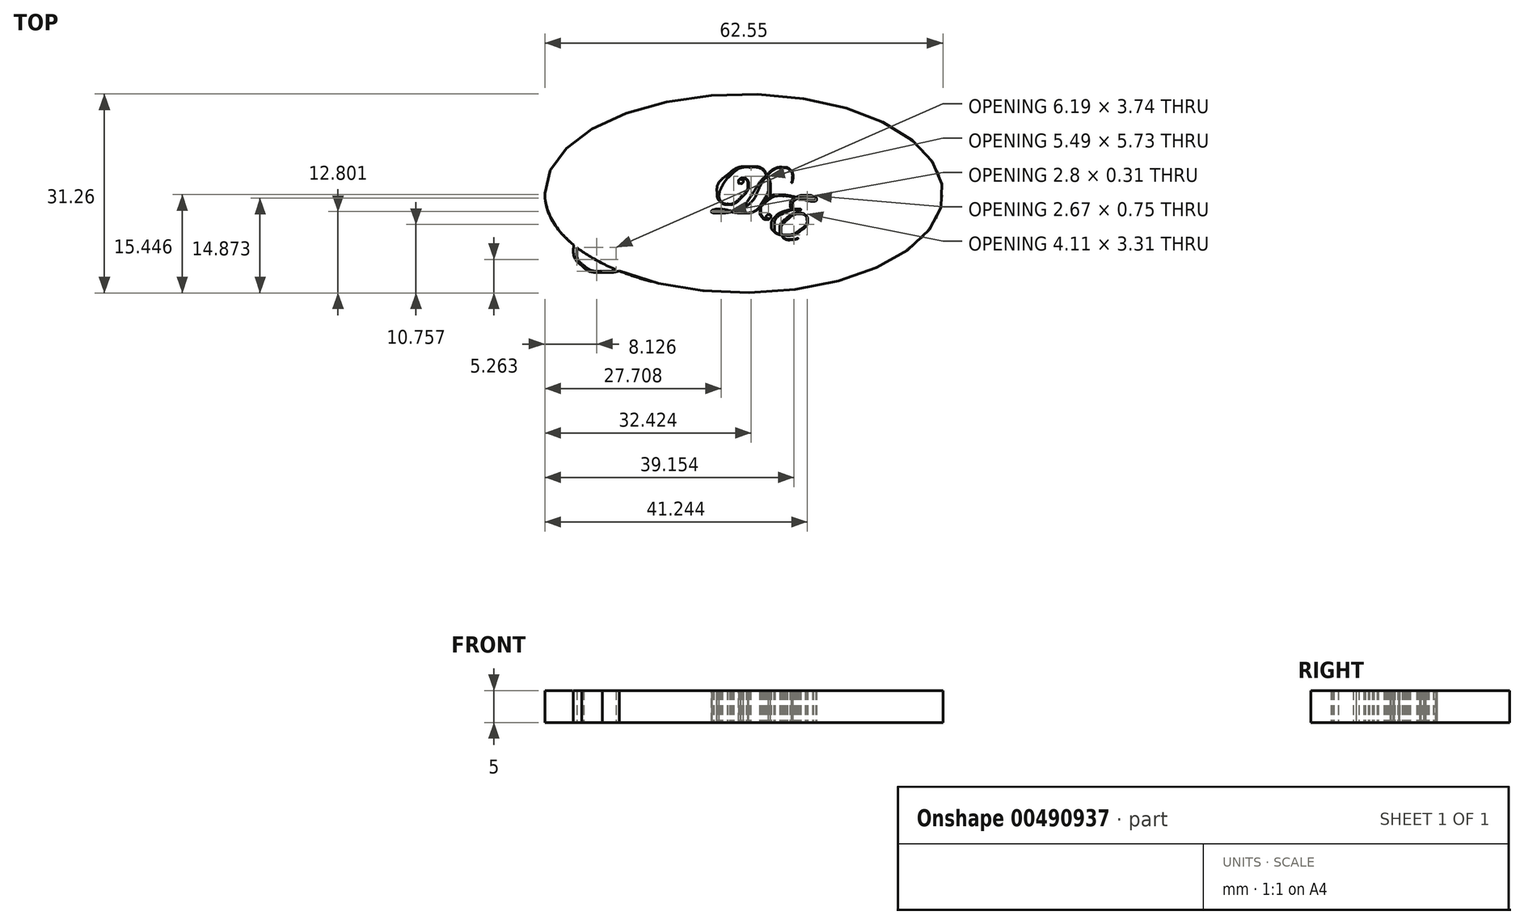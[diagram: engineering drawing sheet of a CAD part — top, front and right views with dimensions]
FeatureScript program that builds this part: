
annotation { "Feature Type Name" : "Feature", "Feature Type Description" : "" }
export const myFeature = defineFeature(function(context is Context, id is Id, definition is map)
    precondition{}
    {
        {
            var Q0;
            Q0=qCreatedBy(makeId("Top.planeOp"),FACE);
            var sketch = newSketch(context, id + "F0", { "sketchPlane" : qUnion([Q0])});
            skFitSpline(sketch, "E0", {"points": [v(-4.56, 0.21) * mm, v(-4.56, 0.16) * mm, v(-4.64, 0.03) * mm, v(-4.81, -0.17) * mm]});
            skFitSpline(sketch, "E1", {"points": [v(-4.81, -0.17) * mm, v(-4.98, -0.37) * mm, v(-5.15, -0.55) * mm, v(-5.33, -0.7) * mm]});
            skFitSpline(sketch, "E2", {"points": [v(-5.33, -0.7) * mm, v(-5.48, -0.94) * mm, v(-5.6, -1.15) * mm, v(-5.67, -1.31) * mm]});
            skFitSpline(sketch, "E3", {"points": [v(-5.67, -1.31) * mm, v(-5.74, -1.47) * mm, v(-5.83, -1.73) * mm, v(-5.94, -2.08) * mm]});
            skFitSpline(sketch, "E4", {"points": [v(-5.94, -2.08) * mm, v(-6.07, -2.51) * mm, v(-6.23, -2.85) * mm, v(-6.43, -3.1) * mm]});
            skFitSpline(sketch, "E5", {"points": [v(-6.43, -3.1) * mm, v(-6.63, -3.36) * mm, v(-6.9, -3.58) * mm, v(-7.25, -3.78) * mm]});
            skFitSpline(sketch, "E6", {"points": [v(-7.25, -3.78) * mm, v(-7.76, -4.06) * mm, v(-8.28, -4.2) * mm, v(-8.81, -4.2) * mm]});
            skFitSpline(sketch, "E7", {"points": [v(-8.81, -4.2) * mm, v(-9.26, -4.2) * mm, v(-9.63, -4.08) * mm, v(-9.9, -3.83) * mm]});
            skFitSpline(sketch, "E8", {"points": [v(-9.9, -3.83) * mm, v(-10.18, -3.59) * mm, v(-10.32, -3.27) * mm, v(-10.32, -2.87) * mm]});
            skFitSpline(sketch, "E9", {"points": [v(-10.32, -2.87) * mm, v(-10.32, -2.53) * mm, v(-10.22, -2.2) * mm, v(-10, -1.9) * mm]});
            skFitSpline(sketch, "E10", {"points": [v(-10, -1.9) * mm, v(-9.8, -1.6) * mm, v(-9.51, -1.35) * mm, v(-9.15, -1.16) * mm]});
            skFitSpline(sketch, "E11", {"points": [v(-9.15, -1.16) * mm, v(-8.78, -0.97) * mm, v(-8.45, -0.88) * mm, v(-8.13, -0.88) * mm]});
            skFitSpline(sketch, "E12", {"points": [v(-8.13, -0.88) * mm, v(-8.1, -0.88) * mm, v(-8.09, -0.88) * mm, v(-8.07, -0.89) * mm]});
            skFitSpline(sketch, "E13", {"points": [v(-8.07, -0.89) * mm, v(-8.07, -0.83) * mm, v(-8.05, -0.73) * mm, v(-8.02, -0.6) * mm]});
            skFitSpline(sketch, "E14", {"points": [v(-8.02, -0.6) * mm, v(-8.06, -0.6) * mm, v(-8.1, -0.6) * mm, v(-8.16, -0.6) * mm]});
            skFitSpline(sketch, "E15", {"points": [v(-8.16, -0.6) * mm, v(-8.51, -0.6) * mm, v(-8.8, -0.53) * mm, v(-9, -0.37) * mm]});
            skFitSpline(sketch, "E16", {"points": [v(-9, -0.37) * mm, v(-9.21, -0.22) * mm, v(-9.32, 0) * mm, v(-9.32, 0.25) * mm]});
            skFitSpline(sketch, "E17", {"points": [v(-9.32, 0.25) * mm, v(-9.32, 0.7) * mm, v(-9.06, 1.1) * mm, v(-8.56, 1.44) * mm]});
            skFitSpline(sketch, "E18", {"points": [v(-8.56, 1.44) * mm, v(-8.05, 1.78) * mm, v(-7.47, 1.96) * mm, v(-6.82, 1.96) * mm]});
            skFitSpline(sketch, "E19", {"points": [v(-6.82, 1.96) * mm, v(-6.3, 1.96) * mm, v(-5.87, 1.83) * mm, v(-5.54, 1.57) * mm]});
            skFitSpline(sketch, "E20", {"points": [v(-5.54, 1.57) * mm, v(-5.3, 1.65) * mm, v(-5.14, 1.7) * mm, v(-5.03, 1.7) * mm]});
            skFitSpline(sketch, "E21", {"points": [v(-5.03, 1.7) * mm, v(-4.82, 1.7) * mm, v(-4.71, 1.6) * mm, v(-4.71, 1.43) * mm]});
            skFitSpline(sketch, "E22", {"points": [v(-4.71, 1.43) * mm, v(-4.71, 1.27) * mm, v(-4.84, 1.07) * mm, v(-5.08, 0.83) * mm]});
            skFitSpline(sketch, "E23", {"points": [v(-5.08, 0.83) * mm, v(-5.07, 0.7) * mm, v(-5.06, 0.6) * mm, v(-5.06, 0.53) * mm]});
            skFitSpline(sketch, "E24", {"points": [v(-5.06, 0.53) * mm, v(-5.06, 0.29) * mm, v(-5.13, 0.04) * mm, v(-5.26, -0.23) * mm]});
            skFitSpline(sketch, "E25", {"points": [v(-5.26, -0.23) * mm, v(-5.3, -0.31) * mm, v(-5.33, -0.35) * mm, v(-5.35, -0.35) * mm]});
            skFitSpline(sketch, "E26", {"points": [v(-5.35, -0.35) * mm, v(-5.36, -0.35) * mm, v(-5.37, -0.35) * mm, v(-5.37, -0.33) * mm]});
            skFitSpline(sketch, "E27", {"points": [v(-5.37, -0.33) * mm, v(-5.37, -0.32) * mm, v(-5.36, -0.31) * mm, v(-5.36, -0.3) * mm]});
            skFitSpline(sketch, "E28", {"points": [v(-5.36, -0.3) * mm, v(-5.2, -0.03) * mm, v(-5.12, 0.25) * mm, v(-5.12, 0.54) * mm]});
            skFitSpline(sketch, "E29", {"points": [v(-5.12, 0.54) * mm, v(-5.12, 0.63) * mm, v(-5.12, 0.71) * mm, v(-5.13, 0.79) * mm]});
            skFitSpline(sketch, "E30", {"points": [v(-5.13, 0.79) * mm, v(-5.5, 0.47) * mm, v(-5.9, 0.19) * mm, v(-6.35, -0.06) * mm]});
            skFitSpline(sketch, "E31", {"points": [v(-6.35, -0.06) * mm, v(-6.8, -0.3) * mm, v(-7.23, -0.46) * mm, v(-7.64, -0.55) * mm]});
            skFitSpline(sketch, "E32", {"points": [v(-7.64, -0.55) * mm, v(-7.7, -0.66) * mm, v(-7.76, -0.78) * mm, v(-7.8, -0.9) * mm]});
            skFitSpline(sketch, "E33", {"points": [v(-7.8, -0.9) * mm, v(-7.22, -1) * mm, v(-6.93, -1.32) * mm, v(-6.93, -1.85) * mm]});
            skFitSpline(sketch, "E34", {"points": [v(-6.93, -1.91) * mm, v(-6.5, -1.8) * mm, v(-5.96, -1.36) * mm, v(-5.33, -0.62) * mm]});
            skFitSpline(sketch, "E35", {"points": [v(-5.33, -0.62) * mm, v(-5.18, -0.4) * mm, v(-5.04, -0.2) * mm, v(-4.89, -0.03) * mm]});
            skFitSpline(sketch, "E36", {"points": [v(-4.89, -0.03) * mm, v(-4.74, 0.14) * mm, v(-4.64, 0.23) * mm, v(-4.58, 0.23) * mm]});
            skFitSpline(sketch, "E37", {"points": [v(-4.58, 0.23) * mm, v(-4.57, 0.23) * mm, v(-4.56, 0.22) * mm, v(-4.56, 0.21) * mm]});
            skLineSegment(sketch, "E38", {"start": v(-6.93, -1.85) * mm, "end": v(-6.93, -1.91) * mm});
            skFitSpline(sketch, "E39", {"points": [v(-4.77, 1.42) * mm, v(-4.77, 1.57) * mm, v(-4.86, 1.64) * mm, v(-5.02, 1.64) * mm]});
            skFitSpline(sketch, "E40", {"points": [v(-5.02, 1.64) * mm, v(-5.15, 1.64) * mm, v(-5.3, 1.6) * mm, v(-5.48, 1.51) * mm]});
            skFitSpline(sketch, "E41", {"points": [v(-5.48, 1.51) * mm, v(-5.3, 1.35) * mm, v(-5.16, 1.14) * mm, v(-5.1, 0.89) * mm]});
            skFitSpline(sketch, "E42", {"points": [v(-5.1, 0.89) * mm, v(-4.88, 1.1) * mm, v(-4.77, 1.28) * mm, v(-4.77, 1.42) * mm]});
            skFitSpline(sketch, "E43", {"points": [v(-5.14, 0.85) * mm, v(-5.2, 1.1) * mm, v(-5.33, 1.32) * mm, v(-5.53, 1.5) * mm]});
            skFitSpline(sketch, "E44", {"points": [v(-5.53, 1.5) * mm, v(-5.92, 1.3) * mm, v(-6.31, 1.02) * mm, v(-6.7, 0.64) * mm]});
            skFitSpline(sketch, "E45", {"points": [v(-6.7, 0.64) * mm, v(-7.09, 0.27) * mm, v(-7.39, -0.1) * mm, v(-7.6, -0.49) * mm]});
            skFitSpline(sketch, "E46", {"points": [v(-7.6, -0.49) * mm, v(-7.21, -0.4) * mm, v(-6.8, -0.23) * mm, v(-6.35, 0.01) * mm]});
            skFitSpline(sketch, "E47", {"points": [v(-6.35, 0.01) * mm, v(-5.9, 0.25) * mm, v(-5.5, 0.53) * mm, v(-5.14, 0.85) * mm]});
            skFitSpline(sketch, "E48", {"points": [v(-5.6, 1.55) * mm, v(-5.9, 1.78) * mm, v(-6.3, 1.9) * mm, v(-6.8, 1.9) * mm]});
            skFitSpline(sketch, "E49", {"points": [v(-6.8, 1.9) * mm, v(-7.42, 1.9) * mm, v(-7.98, 1.72) * mm, v(-8.5, 1.38) * mm]});
            skFitSpline(sketch, "E50", {"points": [v(-8.5, 1.38) * mm, v(-9, 1.04) * mm, v(-9.26, 0.67) * mm, v(-9.26, 0.26) * mm]});
            skFitSpline(sketch, "E51", {"points": [v(-9.26, 0.26) * mm, v(-9.26, 0) * mm, v(-9.16, -0.2) * mm, v(-8.95, -0.33) * mm]});
            skFitSpline(sketch, "E52", {"points": [v(-8.95, -0.33) * mm, v(-8.75, -0.47) * mm, v(-8.47, -0.54) * mm, v(-8.11, -0.54) * mm]});
            skFitSpline(sketch, "E53", {"points": [v(-8, -0.54) * mm, v(-7.74, 0.3) * mm, v(-6.94, 1) * mm, v(-5.6, 1.55) * mm]});
            skLineSegment(sketch, "E54", {"start": v(-8.11, -0.54) * mm, "end": v(-8, -0.54) * mm});
            skFitSpline(sketch, "E55", {"points": [v(-6.99, -1.93) * mm, v(-6.97, -1.67) * mm, v(-7.04, -1.45) * mm, v(-7.18, -1.29) * mm]});
            skFitSpline(sketch, "E56", {"points": [v(-7.18, -1.29) * mm, v(-7.32, -1.12) * mm, v(-7.53, -1) * mm, v(-7.8, -0.96) * mm]});
            skFitSpline(sketch, "E57", {"points": [v(-7.8, -0.96) * mm, v(-7.84, -1.07) * mm, v(-7.85, -1.18) * mm, v(-7.85, -1.3) * mm]});
            skFitSpline(sketch, "E58", {"points": [v(-7.85, -1.3) * mm, v(-7.85, -1.5) * mm, v(-7.79, -1.65) * mm, v(-7.67, -1.77) * mm]});
            skFitSpline(sketch, "E59", {"points": [v(-7.67, -1.77) * mm, v(-7.54, -1.88) * mm, v(-7.37, -1.94) * mm, v(-7.17, -1.94) * mm]});
            skFitSpline(sketch, "E60", {"points": [v(-7.17, -1.94) * mm, v(-7.1, -1.94) * mm, v(-7.04, -1.94) * mm, v(-6.99, -1.93) * mm]});
            skFitSpline(sketch, "E61", {"points": [v(-5.44, -0.83) * mm, v(-6.03, -1.48) * mm, v(-6.53, -1.86) * mm, v(-6.94, -1.98) * mm]});
            skFitSpline(sketch, "E62", {"points": [v(-6.94, -1.98) * mm, v(-6.99, -2.27) * mm, v(-7.13, -2.55) * mm, v(-7.37, -2.8) * mm]});
            skFitSpline(sketch, "E63", {"points": [v(-7.37, -2.8) * mm, v(-7.6, -3.04) * mm, v(-7.84, -3.16) * mm, v(-8.09, -3.16) * mm]});
            skFitSpline(sketch, "E64", {"points": [v(-8.09, -3.16) * mm, v(-8.21, -3.16) * mm, v(-8.32, -3.12) * mm, v(-8.4, -3.04) * mm]});
            skFitSpline(sketch, "E65", {"points": [v(-8.4, -3.04) * mm, v(-8.5, -2.97) * mm, v(-8.54, -2.87) * mm, v(-8.54, -2.75) * mm]});
            skFitSpline(sketch, "E66", {"points": [v(-8.54, -2.75) * mm, v(-8.54, -2.63) * mm, v(-8.5, -2.52) * mm, v(-8.42, -2.43) * mm]});
            skFitSpline(sketch, "E67", {"points": [v(-8.42, -2.43) * mm, v(-8.33, -2.33) * mm, v(-8.24, -2.28) * mm, v(-8.14, -2.28) * mm]});
            skFitSpline(sketch, "E68", {"points": [v(-8.14, -2.28) * mm, v(-7.99, -2.28) * mm, v(-7.91, -2.35) * mm, v(-7.91, -2.5) * mm]});
            skFitSpline(sketch, "E69", {"points": [v(-7.91, -2.5) * mm, v(-7.91, -2.56) * mm, v(-7.94, -2.61) * mm, v(-7.99, -2.66) * mm]});
            skFitSpline(sketch, "E70", {"points": [v(-7.99, -2.66) * mm, v(-8.04, -2.71) * mm, v(-8.1, -2.74) * mm, v(-8.15, -2.74) * mm]});
            skFitSpline(sketch, "E71", {"points": [v(-8.15, -2.74) * mm, v(-8.27, -2.74) * mm, v(-8.33, -2.69) * mm, v(-8.33, -2.59) * mm]});
            skFitSpline(sketch, "E72", {"points": [v(-8.33, -2.59) * mm, v(-8.33, -2.57) * mm, v(-8.32, -2.55) * mm, v(-8.31, -2.51) * mm]});
            skFitSpline(sketch, "E73", {"points": [v(-8.31, -2.51) * mm, v(-8.31, -2.5) * mm, v(-8.3, -2.48) * mm, v(-8.3, -2.46) * mm]});
            skFitSpline(sketch, "E74", {"points": [v(-8.3, -2.46) * mm, v(-8.3, -2.45) * mm, v(-8.31, -2.44) * mm, v(-8.33, -2.44) * mm]});
            skFitSpline(sketch, "E75", {"points": [v(-8.33, -2.44) * mm, v(-8.36, -2.44) * mm, v(-8.4, -2.48) * mm, v(-8.43, -2.55) * mm]});
            skFitSpline(sketch, "E76", {"points": [v(-8.43, -2.55) * mm, v(-8.46, -2.62) * mm, v(-8.48, -2.69) * mm, v(-8.48, -2.75) * mm]});
            skFitSpline(sketch, "E77", {"points": [v(-8.48, -2.75) * mm, v(-8.48, -2.86) * mm, v(-8.44, -2.94) * mm, v(-8.36, -3) * mm]});
            skFitSpline(sketch, "E78", {"points": [v(-8.36, -3) * mm, v(-8.29, -3.08) * mm, v(-8.2, -3.11) * mm, v(-8.09, -3.11) * mm]});
            skFitSpline(sketch, "E79", {"points": [v(-8.09, -3.11) * mm, v(-7.86, -3.11) * mm, v(-7.63, -2.99) * mm, v(-7.4, -2.75) * mm]});
            skFitSpline(sketch, "E80", {"points": [v(-7.4, -2.75) * mm, v(-7.16, -2.5) * mm, v(-7.03, -2.25) * mm, v(-7, -1.99) * mm]});
            skFitSpline(sketch, "E81", {"points": [v(-7, -1.99) * mm, v(-7.05, -2) * mm, v(-7.1, -2) * mm, v(-7.17, -2) * mm]});
            skFitSpline(sketch, "E82", {"points": [v(-7.17, -2) * mm, v(-7.45, -2) * mm, v(-7.67, -1.9) * mm, v(-7.83, -1.72) * mm]});
            skFitSpline(sketch, "E83", {"points": [v(-7.83, -1.72) * mm, v(-8, -1.53) * mm, v(-8.07, -1.27) * mm, v(-8.07, -0.95) * mm]});
            skFitSpline(sketch, "E84", {"points": [v(-8.07, -0.95) * mm, v(-8.62, -0.98) * mm, v(-9.1, -1.21) * mm, v(-9.52, -1.64) * mm]});
            skFitSpline(sketch, "E85", {"points": [v(-9.52, -1.64) * mm, v(-9.93, -2.06) * mm, v(-10.14, -2.54) * mm, v(-10.14, -3.06) * mm]});
            skFitSpline(sketch, "E86", {"points": [v(-10.14, -3.06) * mm, v(-10.14, -3.38) * mm, v(-10.02, -3.64) * mm, v(-9.78, -3.84) * mm]});
            skFitSpline(sketch, "E87", {"points": [v(-9.78, -3.84) * mm, v(-9.55, -4.03) * mm, v(-9.24, -4.13) * mm, v(-8.86, -4.13) * mm]});
            skFitSpline(sketch, "E88", {"points": [v(-8.86, -4.13) * mm, v(-8.34, -4.13) * mm, v(-7.87, -3.95) * mm, v(-7.45, -3.58) * mm]});
            skFitSpline(sketch, "E89", {"points": [v(-7.45, -3.58) * mm, v(-7.03, -3.22) * mm, v(-6.54, -2.57) * mm, v(-5.98, -1.64) * mm]});
            skFitSpline(sketch, "E90", {"points": [v(-5.98, -1.64) * mm, v(-5.81, -1.35) * mm, v(-5.63, -1.08) * mm, v(-5.44, -0.83) * mm]});
            skFitSpline(sketch, "E91", {"points": [v(7.71, 2.56) * mm, v(7.71, 2.38) * mm, v(7.7, 2.2) * mm, v(7.65, 2) * mm]});
            skFitSpline(sketch, "E92", {"points": [v(7.65, 2) * mm, v(7.6, 1.8) * mm, v(7.57, 1.7) * mm, v(7.53, 1.7) * mm]});
            skFitSpline(sketch, "E93", {"points": [v(7.53, 1.7) * mm, v(7.5, 1.7) * mm, v(7.5, 1.71) * mm, v(7.5, 1.73) * mm]});
            skFitSpline(sketch, "E94", {"points": [v(7.5, 1.73) * mm, v(7.5, 1.76) * mm, v(7.5, 1.78) * mm, v(7.5, 1.8) * mm]});
            skFitSpline(sketch, "E95", {"points": [v(7.5, 1.8) * mm, v(7.59, 2.01) * mm, v(7.63, 2.26) * mm, v(7.63, 2.55) * mm]});
            skFitSpline(sketch, "E96", {"points": [v(7.63, 2.55) * mm, v(7.63, 2.99) * mm, v(7.5, 3.34) * mm, v(7.23, 3.6) * mm]});
            skFitSpline(sketch, "E97", {"points": [v(7.23, 3.6) * mm, v(6.96, 3.88) * mm, v(6.6, 4.01) * mm, v(6.17, 4.01) * mm]});
            skFitSpline(sketch, "E98", {"points": [v(6.17, 4.01) * mm, v(5.32, 4.01) * mm, v(4.5, 3.6) * mm, v(3.7, 2.8) * mm]});
            skFitSpline(sketch, "E99", {"points": [v(3.7, 2.8) * mm, v(4.01, 2.25) * mm, v(4.16, 1.66) * mm, v(4.16, 1.03) * mm]});
            skFitSpline(sketch, "E100", {"points": [v(4.16, 1.03) * mm, v(4.16, -0.11) * mm, v(3.72, -1.08) * mm, v(2.84, -1.88) * mm]});
            skFitSpline(sketch, "E101", {"points": [v(2.84, -1.88) * mm, v(1.96, -2.68) * mm, v(0.89, -3.07) * mm, v(-0.38, -3.07) * mm]});
            skFitSpline(sketch, "E102", {"points": [v(-0.38, -3.07) * mm, v(-0.77, -3.07) * mm, v(-1.3, -3.02) * mm, v(-1.99, -2.91) * mm]});
            skFitSpline(sketch, "E103", {"points": [v(-1.99, -2.91) * mm, v(-2.58, -3.02) * mm, v(-3.14, -3.07) * mm, v(-3.69, -3.07) * mm]});
            skFitSpline(sketch, "E104", {"points": [v(-3.69, -3.07) * mm, v(-4.6, -3.07) * mm, v(-5.07, -2.98) * mm, v(-5.07, -2.8) * mm]});
            skFitSpline(sketch, "E105", {"points": [v(-5.07, -2.8) * mm, v(-5.07, -2.7) * mm, v(-4.96, -2.63) * mm, v(-4.73, -2.56) * mm]});
            skFitSpline(sketch, "E106", {"points": [v(-4.73, -2.56) * mm, v(-4.5, -2.49) * mm, v(-4.24, -2.45) * mm, v(-3.94, -2.45) * mm]});
            skFitSpline(sketch, "E107", {"points": [v(-3.94, -2.45) * mm, v(-3.58, -2.45) * mm, v(-2.86, -2.57) * mm, v(-1.77, -2.8) * mm]});
            skFitSpline(sketch, "E108", {"points": [v(-1.77, -2.8) * mm, v(-1.04, -2.62) * mm, v(-0.47, -2.31) * mm, v(-0.05, -1.9) * mm]});
            skFitSpline(sketch, "E109", {"points": [v(-0.05, -1.9) * mm, v(0.36, -1.5) * mm, v(0.99, -0.62) * mm, v(1.83, 0.73) * mm]});
            skFitSpline(sketch, "E110", {"points": [v(1.83, 0.73) * mm, v(2.34, 1.54) * mm, v(2.9, 2.24) * mm, v(3.52, 2.82) * mm]});
            skFitSpline(sketch, "E111", {"points": [v(3.52, 2.82) * mm, v(3, 3.68) * mm, v(2.18, 4.1) * mm, v(1.04, 4.1) * mm]});
            skFitSpline(sketch, "E112", {"points": [v(1.04, 4.1) * mm, v(-0.14, 4.1) * mm, v(-1.23, 3.64) * mm, v(-2.21, 2.71) * mm]});
            skFitSpline(sketch, "E113", {"points": [v(-2.21, 2.71) * mm, v(-2.7, 2.24) * mm, v(-3.1, 1.73) * mm, v(-3.4, 1.16) * mm]});
            skFitSpline(sketch, "E114", {"points": [v(-3.4, 1.16) * mm, v(-3.7, 0.6) * mm, v(-3.85, 0.07) * mm, v(-3.85, -0.4) * mm]});
            skFitSpline(sketch, "E115", {"points": [v(-3.85, -0.4) * mm, v(-3.85, -0.78) * mm, v(-3.73, -1.08) * mm, v(-3.5, -1.3) * mm]});
            skFitSpline(sketch, "E116", {"points": [v(-3.5, -1.3) * mm, v(-3.25, -1.54) * mm, v(-2.93, -1.65) * mm, v(-2.54, -1.65) * mm]});
            skFitSpline(sketch, "E117", {"points": [v(-2.54, -1.65) * mm, v(-1.87, -1.65) * mm, v(-1.18, -1.29) * mm, v(-0.46, -0.57) * mm]});
            skFitSpline(sketch, "E118", {"points": [v(-0.46, -0.57) * mm, v(0.26, 0.15) * mm, v(0.62, 0.84) * mm, v(0.62, 1.5) * mm]});
            skFitSpline(sketch, "E119", {"points": [v(0.62, 1.5) * mm, v(0.62, 1.76) * mm, v(0.55, 1.96) * mm, v(0.4, 2.11) * mm]});
            skFitSpline(sketch, "E120", {"points": [v(0.4, 2.11) * mm, v(0.27, 2.27) * mm, v(0.08, 2.34) * mm, v(-0.14, 2.34) * mm]});
            skFitSpline(sketch, "E121", {"points": [v(-0.14, 2.34) * mm, v(-0.4, 2.34) * mm, v(-0.53, 2.3) * mm, v(-0.53, 2.22) * mm]});
            skFitSpline(sketch, "E122", {"points": [v(-0.53, 2.22) * mm, v(-0.53, 2.2) * mm, v(-0.51, 2.18) * mm, v(-0.47, 2.18) * mm]});
            skFitSpline(sketch, "E123", {"points": [v(-0.47, 2.18) * mm, v(-0.45, 2.18) * mm, v(-0.43, 2.19) * mm, v(-0.42, 2.2) * mm]});
            skFitSpline(sketch, "E124", {"points": [v(-0.35, 2.2) * mm, v(-0.18, 2.2) * mm, v(-0.1, 2.11) * mm, v(-0.1, 1.96) * mm]});
            skFitSpline(sketch, "E125", {"points": [v(-0.1, 1.96) * mm, v(-0.1, 1.84) * mm, v(-0.13, 1.74) * mm, v(-0.22, 1.65) * mm]});
            skFitSpline(sketch, "E126", {"points": [v(-0.22, 1.65) * mm, v(-0.3, 1.57) * mm, v(-0.41, 1.53) * mm, v(-0.53, 1.53) * mm]});
            skFitSpline(sketch, "E127", {"points": [v(-0.53, 1.53) * mm, v(-0.74, 1.53) * mm, v(-0.85, 1.64) * mm, v(-0.85, 1.87) * mm]});
            skFitSpline(sketch, "E128", {"points": [v(-0.85, 1.87) * mm, v(-0.85, 2.03) * mm, v(-0.78, 2.16) * mm, v(-0.64, 2.28) * mm]});
            skFitSpline(sketch, "E129", {"points": [v(-0.64, 2.28) * mm, v(-0.5, 2.39) * mm, v(-0.33, 2.44) * mm, v(-0.13, 2.44) * mm]});
            skFitSpline(sketch, "E130", {"points": [v(-0.13, 2.44) * mm, v(0.12, 2.44) * mm, v(0.33, 2.36) * mm, v(0.49, 2.19) * mm]});
            skFitSpline(sketch, "E131", {"points": [v(0.49, 2.19) * mm, v(0.65, 2.02) * mm, v(0.73, 1.8) * mm, v(0.73, 1.53) * mm]});
            skFitSpline(sketch, "E132", {"points": [v(0.73, 1.53) * mm, v(0.73, 0.82) * mm, v(0.36, 0.1) * mm, v(-0.38, -0.64) * mm]});
            skFitSpline(sketch, "E133", {"points": [v(-0.38, -0.64) * mm, v(-1.11, -1.37) * mm, v(-1.83, -1.74) * mm, v(-2.54, -1.74) * mm]});
            skFitSpline(sketch, "E134", {"points": [v(-2.54, -1.74) * mm, v(-3.02, -1.74) * mm, v(-3.42, -1.58) * mm, v(-3.74, -1.26) * mm]});
            skFitSpline(sketch, "E135", {"points": [v(-3.74, -1.26) * mm, v(-4.05, -0.94) * mm, v(-4.2, -0.52) * mm, v(-4.2, -0.01) * mm]});
            skFitSpline(sketch, "E136", {"points": [v(-4.2, -0.01) * mm, v(-4.2, 1.07) * mm, v(-3.67, 2.05) * mm, v(-2.6, 2.9) * mm]});
            skFitSpline(sketch, "E137", {"points": [v(-2.6, 2.9) * mm, v(-1.53, 3.77) * mm, v(-0.32, 4.2) * mm, v(1.04, 4.2) * mm]});
            skFitSpline(sketch, "E138", {"points": [v(1.04, 4.2) * mm, v(2.19, 4.2) * mm, v(3.05, 3.78) * mm, v(3.64, 2.93) * mm]});
            skFitSpline(sketch, "E139", {"points": [v(3.64, 2.93) * mm, v(4.49, 3.71) * mm, v(5.36, 4.1) * mm, v(6.24, 4.1) * mm]});
            skFitSpline(sketch, "E140", {"points": [v(6.24, 4.1) * mm, v(6.68, 4.1) * mm, v(7.03, 3.96) * mm, v(7.3, 3.68) * mm]});
            skFitSpline(sketch, "E141", {"points": [v(7.3, 3.68) * mm, v(7.58, 3.4) * mm, v(7.71, 3.02) * mm, v(7.71, 2.56) * mm]});
            skLineSegment(sketch, "E142", {"start": v(-0.42, 2.2) * mm, "end": v(-0.35, 2.2) * mm});
            skFitSpline(sketch, "E143", {"points": [v(3.87, 1.42) * mm, v(3.87, 1.87) * mm, v(3.78, 2.29) * mm, v(3.6, 2.68) * mm]});
            skFitSpline(sketch, "E144", {"points": [v(3.6, 2.68) * mm, v(3.12, 2.14) * mm, v(2.7, 1.47) * mm, v(2.33, 0.65) * mm]});
            skFitSpline(sketch, "E145", {"points": [v(2.33, 0.65) * mm, v(1.83, -0.43) * mm, v(1.32, -1.2) * mm, v(0.8, -1.68) * mm]});
            skFitSpline(sketch, "E146", {"points": [v(0.8, -1.68) * mm, v(0.25, -2.17) * mm, v(-0.55, -2.56) * mm, v(-1.6, -2.85) * mm]});
            skFitSpline(sketch, "E147", {"points": [v(-1.6, -2.85) * mm, v(-1.16, -2.94) * mm, v(-0.68, -3) * mm, v(-0.18, -3) * mm]});
            skFitSpline(sketch, "E148", {"points": [v(-0.18, -3) * mm, v(1.15, -3) * mm, v(2.24, -2.34) * mm, v(3.07, -1.05) * mm]});
            skFitSpline(sketch, "E149", {"points": [v(3.07, -1.05) * mm, v(3.6, -0.2) * mm, v(3.87, 0.62) * mm, v(3.87, 1.42) * mm]});
            skFitSpline(sketch, "E150", {"points": [v(-2.17, -2.88) * mm, v(-3.14, -2.74) * mm, v(-3.86, -2.68) * mm, v(-4.33, -2.68) * mm]});
            skFitSpline(sketch, "E151", {"points": [v(-4.33, -2.68) * mm, v(-4.75, -2.68) * mm, v(-4.96, -2.72) * mm, v(-4.96, -2.8) * mm]});
            skFitSpline(sketch, "E152", {"points": [v(-4.96, -2.8) * mm, v(-4.96, -2.92) * mm, v(-4.5, -2.98) * mm, v(-3.59, -2.98) * mm]});
            skFitSpline(sketch, "E153", {"points": [v(-3.59, -2.98) * mm, v(-3.06, -2.98) * mm, v(-2.6, -2.95) * mm, v(-2.17, -2.88) * mm]});
            skFitSpline(sketch, "E154", {"points": [v(10.32, 0.85) * mm, v(10.32, 0.7) * mm, v(10.19, 0.63) * mm, v(9.92, 0.63) * mm]});
            skFitSpline(sketch, "E155", {"points": [v(9.92, 0.63) * mm, v(9.7, 0.63) * mm, v(9.2, 0.73) * mm, v(8.4, 0.92) * mm]});
            skFitSpline(sketch, "E156", {"points": [v(8.4, 0.92) * mm, v(8.03, 0.71) * mm, v(7.85, 0.44) * mm, v(7.85, 0.12) * mm]});
            skFitSpline(sketch, "E157", {"points": [v(7.85, 0.12) * mm, v(7.85, -0.03) * mm, v(7.9, -0.14) * mm, v(8, -0.2) * mm]});
            skFitSpline(sketch, "E158", {"points": [v(8, -0.2) * mm, v(8.16, -0.19) * mm, v(8.28, -0.18) * mm, v(8.36, -0.18) * mm]});
            skFitSpline(sketch, "E159", {"points": [v(8.36, -0.18) * mm, v(8.59, -0.18) * mm, v(8.7, -0.2) * mm, v(8.7, -0.26) * mm]});
            skFitSpline(sketch, "E160", {"points": [v(8.7, -0.26) * mm, v(8.7, -0.3) * mm, v(8.64, -0.31) * mm, v(8.52, -0.31) * mm]});
            skFitSpline(sketch, "E161", {"points": [v(8.52, -0.31) * mm, v(8.37, -0.31) * mm, v(8.2, -0.3) * mm, v(8.02, -0.25) * mm]});
            skFitSpline(sketch, "E162", {"points": [v(8.02, -0.25) * mm, v(7.78, -0.28) * mm, v(7.5, -0.38) * mm, v(7.18, -0.53) * mm]});
            skFitSpline(sketch, "E163", {"points": [v(7.18, -0.53) * mm, v(6.36, -0.92) * mm, v(5.95, -1.43) * mm, v(5.95, -2.05) * mm]});
            skFitSpline(sketch, "E164", {"points": [v(5.95, -2.05) * mm, v(5.95, -2.47) * mm, v(6.17, -2.73) * mm, v(6.62, -2.84) * mm]});
            skFitSpline(sketch, "E165", {"points": [v(6.62, -2.84) * mm, v(6.54, -2.7) * mm, v(6.5, -2.55) * mm, v(6.5, -2.38) * mm]});
            skFitSpline(sketch, "E166", {"points": [v(6.5, -2.38) * mm, v(6.5, -1.95) * mm, v(6.72, -1.55) * mm, v(7.16, -1.19) * mm]});
            skFitSpline(sketch, "E167", {"points": [v(7.16, -1.19) * mm, v(7.6, -0.82) * mm, v(8.08, -0.64) * mm, v(8.6, -0.64) * mm]});
            skFitSpline(sketch, "E168", {"points": [v(8.6, -0.64) * mm, v(8.84, -0.64) * mm, v(9.03, -0.7) * mm, v(9.17, -0.82) * mm]});
            skFitSpline(sketch, "E169", {"points": [v(9.17, -0.82) * mm, v(9.32, -0.94) * mm, v(9.39, -1.1) * mm, v(9.39, -1.3) * mm]});
            skFitSpline(sketch, "E170", {"points": [v(9.39, -1.3) * mm, v(9.39, -1.72) * mm, v(9.15, -2.1) * mm, v(8.69, -2.45) * mm]});
            skFitSpline(sketch, "E171", {"points": [v(8.69, -2.45) * mm, v(8.22, -2.8) * mm, v(7.7, -2.96) * mm, v(7.1, -2.96) * mm]});
            skFitSpline(sketch, "E172", {"points": [v(7.1, -2.96) * mm, v(6.99, -2.96) * mm, v(6.88, -2.96) * mm, v(6.77, -2.94) * mm]});
            skFitSpline(sketch, "E173", {"points": [v(6.77, -2.94) * mm, v(6.98, -3.23) * mm, v(7.3, -3.37) * mm, v(7.7, -3.37) * mm]});
            skFitSpline(sketch, "E174", {"points": [v(7.7, -3.37) * mm, v(7.96, -3.37) * mm, v(8.17, -3.33) * mm, v(8.33, -3.25) * mm]});
            skFitSpline(sketch, "E175", {"points": [v(8.37, -3.25) * mm, v(8.39, -3.25) * mm, v(8.4, -3.26) * mm, v(8.4, -3.27) * mm]});
            skFitSpline(sketch, "E176", {"points": [v(8.4, -3.27) * mm, v(8.4, -3.3) * mm, v(8.31, -3.33) * mm, v(8.15, -3.37) * mm]});
            skFitSpline(sketch, "E177", {"points": [v(8.15, -3.37) * mm, v(7.99, -3.4) * mm, v(7.84, -3.42) * mm, v(7.7, -3.42) * mm]});
            skFitSpline(sketch, "E178", {"points": [v(7.7, -3.42) * mm, v(7.25, -3.42) * mm, v(6.9, -3.25) * mm, v(6.66, -2.92) * mm]});
            skFitSpline(sketch, "E179", {"points": [v(6.66, -2.92) * mm, v(6.33, -2.85) * mm, v(6.06, -2.72) * mm, v(5.87, -2.55) * mm]});
            skFitSpline(sketch, "E180", {"points": [v(5.87, -2.55) * mm, v(5.69, -2.37) * mm, v(5.6, -2.16) * mm, v(5.6, -1.92) * mm]});
            skFitSpline(sketch, "E181", {"points": [v(5.6, -1.92) * mm, v(5.6, -1.6) * mm, v(5.72, -1.3) * mm, v(5.99, -1.03) * mm]});
            skFitSpline(sketch, "E182", {"points": [v(5.99, -1.03) * mm, v(6.25, -0.76) * mm, v(6.6, -0.55) * mm, v(7.04, -0.4) * mm]});
            skFitSpline(sketch, "E183", {"points": [v(7.04, -0.4) * mm, v(7.3, -0.32) * mm, v(7.6, -0.25) * mm, v(7.94, -0.21) * mm]});
            skFitSpline(sketch, "E184", {"points": [v(7.94, -0.21) * mm, v(7.7, -0.11) * mm, v(7.58, 0.05) * mm, v(7.58, 0.28) * mm]});
            skFitSpline(sketch, "E185", {"points": [v(7.58, 0.28) * mm, v(7.58, 0.56) * mm, v(7.76, 0.8) * mm, v(8.11, 1) * mm]});
            skFitSpline(sketch, "E186", {"points": [v(8.11, 1) * mm, v(7.6, 1.12) * mm, v(7.18, 1.18) * mm, v(6.85, 1.18) * mm]});
            skFitSpline(sketch, "E187", {"points": [v(6.85, 1.18) * mm, v(6.2, 1.18) * mm, v(5.65, 1.02) * mm, v(5.2, 0.7) * mm]});
            skFitSpline(sketch, "E188", {"points": [v(5.2, 0.7) * mm, v(4.74, 0.37) * mm, v(4.51, -0.02) * mm, v(4.51, -0.48) * mm]});
            skFitSpline(sketch, "E189", {"points": [v(4.51, -0.48) * mm, v(4.51, -0.69) * mm, v(4.58, -0.86) * mm, v(4.7, -1.01) * mm]});
            skFitSpline(sketch, "E190", {"points": [v(4.7, -1.01) * mm, v(4.82, -1.16) * mm, v(4.96, -1.23) * mm, v(5.13, -1.23) * mm]});
            skFitSpline(sketch, "E191", {"points": [v(5.13, -1.23) * mm, v(5.24, -1.23) * mm, v(5.3, -1.21) * mm, v(5.3, -1.17) * mm]});
            skFitSpline(sketch, "E192", {"points": [v(5.3, -1.17) * mm, v(5.3, -1.15) * mm, v(5.28, -1.15) * mm, v(5.24, -1.15) * mm]});
            skFitSpline(sketch, "E193", {"points": [v(5.24, -1.15) * mm, v(5.12, -1.15) * mm, v(5.07, -1.1) * mm, v(5.07, -1) * mm]});
            skFitSpline(sketch, "E194", {"points": [v(5.07, -1) * mm, v(5.07, -0.93) * mm, v(5.1, -0.88) * mm, v(5.14, -0.84) * mm]});
            skFitSpline(sketch, "E195", {"points": [v(5.14, -0.84) * mm, v(5.2, -0.8) * mm, v(5.26, -0.77) * mm, v(5.33, -0.77) * mm]});
            skFitSpline(sketch, "E196", {"points": [v(5.33, -0.77) * mm, v(5.47, -0.77) * mm, v(5.54, -0.84) * mm, v(5.54, -0.97) * mm]});
            skFitSpline(sketch, "E197", {"points": [v(5.54, -0.97) * mm, v(5.54, -1.06) * mm, v(5.5, -1.14) * mm, v(5.42, -1.2) * mm]});
            skFitSpline(sketch, "E198", {"points": [v(5.42, -1.2) * mm, v(5.34, -1.27) * mm, v(5.24, -1.3) * mm, v(5.13, -1.3) * mm]});
            skFitSpline(sketch, "E199", {"points": [v(5.13, -1.3) * mm, v(4.93, -1.3) * mm, v(4.75, -1.2) * mm, v(4.6, -1.02) * mm]});
            skFitSpline(sketch, "E200", {"points": [v(4.6, -1.02) * mm, v(4.46, -0.84) * mm, v(4.4, -0.62) * mm, v(4.4, -0.36) * mm]});
            skFitSpline(sketch, "E201", {"points": [v(4.4, -0.36) * mm, v(4.4, 0.03) * mm, v(4.56, 0.38) * mm, v(4.9, 0.7) * mm]});
            skFitSpline(sketch, "E202", {"points": [v(4.9, 0.7) * mm, v(5.3, 1.1) * mm, v(5.86, 1.28) * mm, v(6.59, 1.28) * mm]});
            skFitSpline(sketch, "E203", {"points": [v(6.59, 1.28) * mm, v(6.99, 1.28) * mm, v(7.52, 1.2) * mm, v(8.2, 1.04) * mm]});
            skFitSpline(sketch, "E204", {"points": [v(8.2, 1.04) * mm, v(8.5, 1.18) * mm, v(8.85, 1.26) * mm, v(9.25, 1.26) * mm]});
            skFitSpline(sketch, "E205", {"points": [v(9.25, 1.26) * mm, v(9.54, 1.26) * mm, v(9.8, 1.22) * mm, v(10, 1.14) * mm]});
            skFitSpline(sketch, "E206", {"points": [v(10, 1.14) * mm, v(10.22, 1.06) * mm, v(10.32, 0.96) * mm, v(10.32, 0.85) * mm]});
            skLineSegment(sketch, "E207", {"start": v(8.33, -3.25) * mm, "end": v(8.37, -3.25) * mm});
            skFitSpline(sketch, "E208", {"points": [v(10.25, 0.85) * mm, v(10.25, 0.94) * mm, v(10.16, 1.01) * mm, v(9.98, 1.08) * mm]});
            skFitSpline(sketch, "E209", {"points": [v(9.98, 1.08) * mm, v(9.8, 1.15) * mm, v(9.6, 1.18) * mm, v(9.36, 1.18) * mm]});
            skFitSpline(sketch, "E210", {"points": [v(9.36, 1.18) * mm, v(9.04, 1.18) * mm, v(8.75, 1.1) * mm, v(8.48, 0.97) * mm]});
            skFitSpline(sketch, "E211", {"points": [v(8.48, 0.97) * mm, v(9.06, 0.78) * mm, v(9.55, 0.69) * mm, v(9.95, 0.69) * mm]});
            skFitSpline(sketch, "E212", {"points": [v(9.95, 0.69) * mm, v(10.15, 0.69) * mm, v(10.25, 0.74) * mm, v(10.25, 0.85) * mm]});
            skFitSpline(sketch, "E213", {"points": [v(9.33, -1.27) * mm, v(9.33, -1.11) * mm, v(9.27, -0.98) * mm, v(9.14, -0.88) * mm]});
            skFitSpline(sketch, "E214", {"points": [v(9.14, -0.88) * mm, v(9.02, -0.78) * mm, v(8.86, -0.72) * mm, v(8.67, -0.72) * mm]});
            skFitSpline(sketch, "E215", {"points": [v(8.67, -0.72) * mm, v(8.2, -0.72) * mm, v(7.74, -0.92) * mm, v(7.3, -1.31) * mm]});
            skFitSpline(sketch, "E216", {"points": [v(7.3, -1.31) * mm, v(6.84, -1.7) * mm, v(6.62, -2.1) * mm, v(6.62, -2.5) * mm]});
            skFitSpline(sketch, "E217", {"points": [v(6.62, -2.5) * mm, v(6.62, -2.62) * mm, v(6.65, -2.75) * mm, v(6.73, -2.87) * mm]});
            skFitSpline(sketch, "E218", {"points": [v(6.73, -2.87) * mm, v(6.85, -2.9) * mm, v(6.97, -2.9) * mm, v(7.08, -2.9) * mm]});
            skFitSpline(sketch, "E219", {"points": [v(7.08, -2.9) * mm, v(7.6, -2.9) * mm, v(8.1, -2.73) * mm, v(8.6, -2.37) * mm]});
            skFitSpline(sketch, "E220", {"points": [v(8.6, -2.37) * mm, v(9.08, -2.01) * mm, v(9.33, -1.64) * mm, v(9.33, -1.27) * mm]});
            skSolve(sketch);
        }
        {
            var Q0;
            Q0=makeQuery(id+"F0.imprint","IMPRINT",FACE,{"disambiguationData":[TD([[makeQuery(id+"F0.imprint","IMPRINT",EDGE,{"derivedFrom":sQuery(id+"F0.wireOp",EDGE,"E91")}),-1.0]])]});
            var Q1;
            Q1=makeQuery(id+"F0.imprint","IMPRINT",FACE,{"disambiguationData":[TD([[makeQuery(id+"F0.imprint","IMPRINT",EDGE,{"derivedFrom":sQuery(id+"F0.wireOp",EDGE,"E0")}),-1.0]])]});
            var Q2;
            Q2=makeQuery(id+"F0.imprint","IMPRINT",FACE,{"disambiguationData":[TD([[makeQuery(id+"F0.imprint","IMPRINT",EDGE,{"derivedFrom":sQuery(id+"F0.wireOp",EDGE,"E154")}),-1.0]])]});
            extrude(context, id + "F1", {"entities" : qUnion([Q0, Q1, Q2]), "depth" : 5 * mm});
        }
        {
            var Q0;
            Q0=makeQuery(id+"F1.opExtrude","SWEPT_BODY",BODY,{"disambiguationData":[OSD([sQuery(id+"F0.wireOp",EDGE,"E0"),sQuery(id+"F0.wireOp",EDGE,"E1"),sQuery(id+"F0.wireOp",EDGE,"E2"),sQuery(id+"F0.wireOp",EDGE,"E3"),sQuery(id+"F0.wireOp",EDGE,"E4"),sQuery(id+"F0.wireOp",EDGE,"E5"),sQuery(id+"F0.wireOp",EDGE,"E6"),sQuery(id+"F0.wireOp",EDGE,"E7"),sQuery(id+"F0.wireOp",EDGE,"E8"),sQuery(id+"F0.wireOp",EDGE,"E9"),sQuery(id+"F0.wireOp",EDGE,"E10"),sQuery(id+"F0.wireOp",EDGE,"E11"),sQuery(id+"F0.wireOp",EDGE,"E12"),sQuery(id+"F0.wireOp",EDGE,"E13"),sQuery(id+"F0.wireOp",EDGE,"E14"),sQuery(id+"F0.wireOp",EDGE,"E15"),sQuery(id+"F0.wireOp",EDGE,"E16"),sQuery(id+"F0.wireOp",EDGE,"E17"),sQuery(id+"F0.wireOp",EDGE,"E18"),sQuery(id+"F0.wireOp",EDGE,"E19"),sQuery(id+"F0.wireOp",EDGE,"E20"),sQuery(id+"F0.wireOp",EDGE,"E21"),sQuery(id+"F0.wireOp",EDGE,"E22"),sQuery(id+"F0.wireOp",EDGE,"E23"),sQuery(id+"F0.wireOp",EDGE,"E24"),sQuery(id+"F0.wireOp",EDGE,"E25"),sQuery(id+"F0.wireOp",EDGE,"E26"),sQuery(id+"F0.wireOp",EDGE,"E27"),sQuery(id+"F0.wireOp",EDGE,"E28"),sQuery(id+"F0.wireOp",EDGE,"E29"),sQuery(id+"F0.wireOp",EDGE,"E30"),sQuery(id+"F0.wireOp",EDGE,"E31"),sQuery(id+"F0.wireOp",EDGE,"E32"),sQuery(id+"F0.wireOp",EDGE,"E33"),sQuery(id+"F0.wireOp",EDGE,"E34"),sQuery(id+"F0.wireOp",EDGE,"E35"),sQuery(id+"F0.wireOp",EDGE,"E36"),sQuery(id+"F0.wireOp",EDGE,"E37"),sQuery(id+"F0.wireOp",EDGE,"E38"),sQuery(id+"F0.wireOp",EDGE,"E39"),sQuery(id+"F0.wireOp",EDGE,"E40"),sQuery(id+"F0.wireOp",EDGE,"E41"),sQuery(id+"F0.wireOp",EDGE,"E42"),sQuery(id+"F0.wireOp",EDGE,"E43"),sQuery(id+"F0.wireOp",EDGE,"E44"),sQuery(id+"F0.wireOp",EDGE,"E45"),sQuery(id+"F0.wireOp",EDGE,"E46"),sQuery(id+"F0.wireOp",EDGE,"E47"),sQuery(id+"F0.wireOp",EDGE,"E48"),sQuery(id+"F0.wireOp",EDGE,"E49"),sQuery(id+"F0.wireOp",EDGE,"E50"),sQuery(id+"F0.wireOp",EDGE,"E51"),sQuery(id+"F0.wireOp",EDGE,"E52"),sQuery(id+"F0.wireOp",EDGE,"E53"),sQuery(id+"F0.wireOp",EDGE,"E54"),sQuery(id+"F0.wireOp",EDGE,"E55"),sQuery(id+"F0.wireOp",EDGE,"E56"),sQuery(id+"F0.wireOp",EDGE,"E57"),sQuery(id+"F0.wireOp",EDGE,"E58"),sQuery(id+"F0.wireOp",EDGE,"E59"),sQuery(id+"F0.wireOp",EDGE,"E60"),sQuery(id+"F0.wireOp",EDGE,"E61"),sQuery(id+"F0.wireOp",EDGE,"E62"),sQuery(id+"F0.wireOp",EDGE,"E63"),sQuery(id+"F0.wireOp",EDGE,"E64"),sQuery(id+"F0.wireOp",EDGE,"E65"),sQuery(id+"F0.wireOp",EDGE,"E66"),sQuery(id+"F0.wireOp",EDGE,"E67"),sQuery(id+"F0.wireOp",EDGE,"E68"),sQuery(id+"F0.wireOp",EDGE,"E69"),sQuery(id+"F0.wireOp",EDGE,"E70"),sQuery(id+"F0.wireOp",EDGE,"E71"),sQuery(id+"F0.wireOp",EDGE,"E72"),sQuery(id+"F0.wireOp",EDGE,"E73"),sQuery(id+"F0.wireOp",EDGE,"E74"),sQuery(id+"F0.wireOp",EDGE,"E75"),sQuery(id+"F0.wireOp",EDGE,"E76"),sQuery(id+"F0.wireOp",EDGE,"E77"),sQuery(id+"F0.wireOp",EDGE,"E78"),sQuery(id+"F0.wireOp",EDGE,"E79"),sQuery(id+"F0.wireOp",EDGE,"E80"),sQuery(id+"F0.wireOp",EDGE,"E81"),sQuery(id+"F0.wireOp",EDGE,"E82"),sQuery(id+"F0.wireOp",EDGE,"E83"),sQuery(id+"F0.wireOp",EDGE,"E84"),sQuery(id+"F0.wireOp",EDGE,"E85"),sQuery(id+"F0.wireOp",EDGE,"E86"),sQuery(id+"F0.wireOp",EDGE,"E87"),sQuery(id+"F0.wireOp",EDGE,"E88"),sQuery(id+"F0.wireOp",EDGE,"E89"),sQuery(id+"F0.wireOp",EDGE,"E90")])]});
            transform(context, id + "F2", {"entities" : qUnion([Q0]), "transformType" : TransformType.TRANSLATION_3D, "dx" : 0.76 * mm, "dy" : -0.89 * mm, "dz" : 0 * mm, "makeCopy" : false});
        }
        {
            var Q0;
            Q0=makeQuery(id+"F1.opExtrude","SWEPT_BODY",BODY,{"disambiguationData":[OSD([sQuery(id+"F0.wireOp",EDGE,"E154"),sQuery(id+"F0.wireOp",EDGE,"E155"),sQuery(id+"F0.wireOp",EDGE,"E156"),sQuery(id+"F0.wireOp",EDGE,"E157"),sQuery(id+"F0.wireOp",EDGE,"E158"),sQuery(id+"F0.wireOp",EDGE,"E159"),sQuery(id+"F0.wireOp",EDGE,"E160"),sQuery(id+"F0.wireOp",EDGE,"E161"),sQuery(id+"F0.wireOp",EDGE,"E162"),sQuery(id+"F0.wireOp",EDGE,"E163"),sQuery(id+"F0.wireOp",EDGE,"E164"),sQuery(id+"F0.wireOp",EDGE,"E165"),sQuery(id+"F0.wireOp",EDGE,"E166"),sQuery(id+"F0.wireOp",EDGE,"E167"),sQuery(id+"F0.wireOp",EDGE,"E168"),sQuery(id+"F0.wireOp",EDGE,"E169"),sQuery(id+"F0.wireOp",EDGE,"E170"),sQuery(id+"F0.wireOp",EDGE,"E171"),sQuery(id+"F0.wireOp",EDGE,"E172"),sQuery(id+"F0.wireOp",EDGE,"E173"),sQuery(id+"F0.wireOp",EDGE,"E174"),sQuery(id+"F0.wireOp",EDGE,"E175"),sQuery(id+"F0.wireOp",EDGE,"E176"),sQuery(id+"F0.wireOp",EDGE,"E177"),sQuery(id+"F0.wireOp",EDGE,"E178"),sQuery(id+"F0.wireOp",EDGE,"E179"),sQuery(id+"F0.wireOp",EDGE,"E180"),sQuery(id+"F0.wireOp",EDGE,"E181"),sQuery(id+"F0.wireOp",EDGE,"E182"),sQuery(id+"F0.wireOp",EDGE,"E183"),sQuery(id+"F0.wireOp",EDGE,"E184"),sQuery(id+"F0.wireOp",EDGE,"E185"),sQuery(id+"F0.wireOp",EDGE,"E186"),sQuery(id+"F0.wireOp",EDGE,"E187"),sQuery(id+"F0.wireOp",EDGE,"E188"),sQuery(id+"F0.wireOp",EDGE,"E189"),sQuery(id+"F0.wireOp",EDGE,"E190"),sQuery(id+"F0.wireOp",EDGE,"E191"),sQuery(id+"F0.wireOp",EDGE,"E192"),sQuery(id+"F0.wireOp",EDGE,"E193"),sQuery(id+"F0.wireOp",EDGE,"E194"),sQuery(id+"F0.wireOp",EDGE,"E195"),sQuery(id+"F0.wireOp",EDGE,"E196"),sQuery(id+"F0.wireOp",EDGE,"E197"),sQuery(id+"F0.wireOp",EDGE,"E198"),sQuery(id+"F0.wireOp",EDGE,"E199"),sQuery(id+"F0.wireOp",EDGE,"E200"),sQuery(id+"F0.wireOp",EDGE,"E201"),sQuery(id+"F0.wireOp",EDGE,"E202"),sQuery(id+"F0.wireOp",EDGE,"E203"),sQuery(id+"F0.wireOp",EDGE,"E204"),sQuery(id+"F0.wireOp",EDGE,"E205"),sQuery(id+"F0.wireOp",EDGE,"E206"),sQuery(id+"F0.wireOp",EDGE,"E207"),sQuery(id+"F0.wireOp",EDGE,"E208"),sQuery(id+"F0.wireOp",EDGE,"E209"),sQuery(id+"F0.wireOp",EDGE,"E210"),sQuery(id+"F0.wireOp",EDGE,"E211"),sQuery(id+"F0.wireOp",EDGE,"E212"),sQuery(id+"F0.wireOp",EDGE,"E213"),sQuery(id+"F0.wireOp",EDGE,"E214"),sQuery(id+"F0.wireOp",EDGE,"E215"),sQuery(id+"F0.wireOp",EDGE,"E216"),sQuery(id+"F0.wireOp",EDGE,"E217"),sQuery(id+"F0.wireOp",EDGE,"E218"),sQuery(id+"F0.wireOp",EDGE,"E219"),sQuery(id+"F0.wireOp",EDGE,"E220")])]});
            transform(context, id + "F3", {"entities" : qUnion([Q0]), "transformType" : TransformType.TRANSLATION_3D, "dx" : -1.26 * mm, "dy" : -1.1 * mm, "dz" : 0 * mm, "makeCopy" : false});
        }
        {
            var Q0;
            Q0=makeQuery(id+"F1.opExtrude","SWEPT_BODY",BODY,{"disambiguationData":[OSD([sQuery(id+"F0.wireOp",EDGE,"E0"),sQuery(id+"F0.wireOp",EDGE,"E1"),sQuery(id+"F0.wireOp",EDGE,"E2"),sQuery(id+"F0.wireOp",EDGE,"E3"),sQuery(id+"F0.wireOp",EDGE,"E4"),sQuery(id+"F0.wireOp",EDGE,"E5"),sQuery(id+"F0.wireOp",EDGE,"E6"),sQuery(id+"F0.wireOp",EDGE,"E7"),sQuery(id+"F0.wireOp",EDGE,"E8"),sQuery(id+"F0.wireOp",EDGE,"E9"),sQuery(id+"F0.wireOp",EDGE,"E10"),sQuery(id+"F0.wireOp",EDGE,"E11"),sQuery(id+"F0.wireOp",EDGE,"E12"),sQuery(id+"F0.wireOp",EDGE,"E13"),sQuery(id+"F0.wireOp",EDGE,"E14"),sQuery(id+"F0.wireOp",EDGE,"E15"),sQuery(id+"F0.wireOp",EDGE,"E16"),sQuery(id+"F0.wireOp",EDGE,"E17"),sQuery(id+"F0.wireOp",EDGE,"E18"),sQuery(id+"F0.wireOp",EDGE,"E19"),sQuery(id+"F0.wireOp",EDGE,"E20"),sQuery(id+"F0.wireOp",EDGE,"E21"),sQuery(id+"F0.wireOp",EDGE,"E22"),sQuery(id+"F0.wireOp",EDGE,"E23"),sQuery(id+"F0.wireOp",EDGE,"E24"),sQuery(id+"F0.wireOp",EDGE,"E25"),sQuery(id+"F0.wireOp",EDGE,"E26"),sQuery(id+"F0.wireOp",EDGE,"E27"),sQuery(id+"F0.wireOp",EDGE,"E28"),sQuery(id+"F0.wireOp",EDGE,"E29"),sQuery(id+"F0.wireOp",EDGE,"E30"),sQuery(id+"F0.wireOp",EDGE,"E31"),sQuery(id+"F0.wireOp",EDGE,"E32"),sQuery(id+"F0.wireOp",EDGE,"E33"),sQuery(id+"F0.wireOp",EDGE,"E34"),sQuery(id+"F0.wireOp",EDGE,"E35"),sQuery(id+"F0.wireOp",EDGE,"E36"),sQuery(id+"F0.wireOp",EDGE,"E37"),sQuery(id+"F0.wireOp",EDGE,"E38"),sQuery(id+"F0.wireOp",EDGE,"E39"),sQuery(id+"F0.wireOp",EDGE,"E40"),sQuery(id+"F0.wireOp",EDGE,"E41"),sQuery(id+"F0.wireOp",EDGE,"E42"),sQuery(id+"F0.wireOp",EDGE,"E43"),sQuery(id+"F0.wireOp",EDGE,"E44"),sQuery(id+"F0.wireOp",EDGE,"E45"),sQuery(id+"F0.wireOp",EDGE,"E46"),sQuery(id+"F0.wireOp",EDGE,"E47"),sQuery(id+"F0.wireOp",EDGE,"E48"),sQuery(id+"F0.wireOp",EDGE,"E49"),sQuery(id+"F0.wireOp",EDGE,"E50"),sQuery(id+"F0.wireOp",EDGE,"E51"),sQuery(id+"F0.wireOp",EDGE,"E52"),sQuery(id+"F0.wireOp",EDGE,"E53"),sQuery(id+"F0.wireOp",EDGE,"E54"),sQuery(id+"F0.wireOp",EDGE,"E55"),sQuery(id+"F0.wireOp",EDGE,"E56"),sQuery(id+"F0.wireOp",EDGE,"E57"),sQuery(id+"F0.wireOp",EDGE,"E58"),sQuery(id+"F0.wireOp",EDGE,"E59"),sQuery(id+"F0.wireOp",EDGE,"E60"),sQuery(id+"F0.wireOp",EDGE,"E61"),sQuery(id+"F0.wireOp",EDGE,"E62"),sQuery(id+"F0.wireOp",EDGE,"E63"),sQuery(id+"F0.wireOp",EDGE,"E64"),sQuery(id+"F0.wireOp",EDGE,"E65"),sQuery(id+"F0.wireOp",EDGE,"E66"),sQuery(id+"F0.wireOp",EDGE,"E67"),sQuery(id+"F0.wireOp",EDGE,"E68"),sQuery(id+"F0.wireOp",EDGE,"E69"),sQuery(id+"F0.wireOp",EDGE,"E70"),sQuery(id+"F0.wireOp",EDGE,"E71"),sQuery(id+"F0.wireOp",EDGE,"E72"),sQuery(id+"F0.wireOp",EDGE,"E73"),sQuery(id+"F0.wireOp",EDGE,"E74"),sQuery(id+"F0.wireOp",EDGE,"E75"),sQuery(id+"F0.wireOp",EDGE,"E76"),sQuery(id+"F0.wireOp",EDGE,"E77"),sQuery(id+"F0.wireOp",EDGE,"E78"),sQuery(id+"F0.wireOp",EDGE,"E79"),sQuery(id+"F0.wireOp",EDGE,"E80"),sQuery(id+"F0.wireOp",EDGE,"E81"),sQuery(id+"F0.wireOp",EDGE,"E82"),sQuery(id+"F0.wireOp",EDGE,"E83"),sQuery(id+"F0.wireOp",EDGE,"E84"),sQuery(id+"F0.wireOp",EDGE,"E85"),sQuery(id+"F0.wireOp",EDGE,"E86"),sQuery(id+"F0.wireOp",EDGE,"E87"),sQuery(id+"F0.wireOp",EDGE,"E88"),sQuery(id+"F0.wireOp",EDGE,"E89"),sQuery(id+"F0.wireOp",EDGE,"E90")])]});
            var Q1;
            Q1=qCreatedBy(makeId("Origin.pointOp"),VERTEX);
            transform(context, id + "F4", {"entities" : qUnion([Q0]), "transformType" : TransformType.SCALE_UNIFORMLY, "scale" : 1.25, "scalePoint" : qUnion([Q1]), "makeCopy" : false});
        }
        {
            var Q0;
            Q0=makeQuery(id+"F1.opExtrude","SWEPT_BODY",BODY,{"disambiguationData":[OSD([sQuery(id+"F0.wireOp",EDGE,"E154"),sQuery(id+"F0.wireOp",EDGE,"E155"),sQuery(id+"F0.wireOp",EDGE,"E156"),sQuery(id+"F0.wireOp",EDGE,"E157"),sQuery(id+"F0.wireOp",EDGE,"E158"),sQuery(id+"F0.wireOp",EDGE,"E159"),sQuery(id+"F0.wireOp",EDGE,"E160"),sQuery(id+"F0.wireOp",EDGE,"E161"),sQuery(id+"F0.wireOp",EDGE,"E162"),sQuery(id+"F0.wireOp",EDGE,"E163"),sQuery(id+"F0.wireOp",EDGE,"E164"),sQuery(id+"F0.wireOp",EDGE,"E165"),sQuery(id+"F0.wireOp",EDGE,"E166"),sQuery(id+"F0.wireOp",EDGE,"E167"),sQuery(id+"F0.wireOp",EDGE,"E168"),sQuery(id+"F0.wireOp",EDGE,"E169"),sQuery(id+"F0.wireOp",EDGE,"E170"),sQuery(id+"F0.wireOp",EDGE,"E171"),sQuery(id+"F0.wireOp",EDGE,"E172"),sQuery(id+"F0.wireOp",EDGE,"E173"),sQuery(id+"F0.wireOp",EDGE,"E174"),sQuery(id+"F0.wireOp",EDGE,"E175"),sQuery(id+"F0.wireOp",EDGE,"E176"),sQuery(id+"F0.wireOp",EDGE,"E177"),sQuery(id+"F0.wireOp",EDGE,"E178"),sQuery(id+"F0.wireOp",EDGE,"E179"),sQuery(id+"F0.wireOp",EDGE,"E180"),sQuery(id+"F0.wireOp",EDGE,"E181"),sQuery(id+"F0.wireOp",EDGE,"E182"),sQuery(id+"F0.wireOp",EDGE,"E183"),sQuery(id+"F0.wireOp",EDGE,"E184"),sQuery(id+"F0.wireOp",EDGE,"E185"),sQuery(id+"F0.wireOp",EDGE,"E186"),sQuery(id+"F0.wireOp",EDGE,"E187"),sQuery(id+"F0.wireOp",EDGE,"E188"),sQuery(id+"F0.wireOp",EDGE,"E189"),sQuery(id+"F0.wireOp",EDGE,"E190"),sQuery(id+"F0.wireOp",EDGE,"E191"),sQuery(id+"F0.wireOp",EDGE,"E192"),sQuery(id+"F0.wireOp",EDGE,"E193"),sQuery(id+"F0.wireOp",EDGE,"E194"),sQuery(id+"F0.wireOp",EDGE,"E195"),sQuery(id+"F0.wireOp",EDGE,"E196"),sQuery(id+"F0.wireOp",EDGE,"E197"),sQuery(id+"F0.wireOp",EDGE,"E198"),sQuery(id+"F0.wireOp",EDGE,"E199"),sQuery(id+"F0.wireOp",EDGE,"E200"),sQuery(id+"F0.wireOp",EDGE,"E201"),sQuery(id+"F0.wireOp",EDGE,"E202"),sQuery(id+"F0.wireOp",EDGE,"E203"),sQuery(id+"F0.wireOp",EDGE,"E204"),sQuery(id+"F0.wireOp",EDGE,"E205"),sQuery(id+"F0.wireOp",EDGE,"E206"),sQuery(id+"F0.wireOp",EDGE,"E207"),sQuery(id+"F0.wireOp",EDGE,"E208"),sQuery(id+"F0.wireOp",EDGE,"E209"),sQuery(id+"F0.wireOp",EDGE,"E210"),sQuery(id+"F0.wireOp",EDGE,"E211"),sQuery(id+"F0.wireOp",EDGE,"E212"),sQuery(id+"F0.wireOp",EDGE,"E213"),sQuery(id+"F0.wireOp",EDGE,"E214"),sQuery(id+"F0.wireOp",EDGE,"E215"),sQuery(id+"F0.wireOp",EDGE,"E216"),sQuery(id+"F0.wireOp",EDGE,"E217"),sQuery(id+"F0.wireOp",EDGE,"E218"),sQuery(id+"F0.wireOp",EDGE,"E219"),sQuery(id+"F0.wireOp",EDGE,"E220")])]});
            var Q1;
            Q1=qCreatedBy(makeId("Origin.pointOp"),VERTEX);
            transform(context, id + "F5", {"entities" : qUnion([Q0]), "transformType" : TransformType.SCALE_UNIFORMLY, "scale" : 1.5, "scalePoint" : qUnion([Q1]), "makeCopy" : false});
        }
        {
            var Q0;
            Q0=makeQuery(id+"F1.opExtrude","SWEPT_BODY",BODY,{"disambiguationData":[OSD([sQuery(id+"F0.wireOp",EDGE,"E0"),sQuery(id+"F0.wireOp",EDGE,"E1"),sQuery(id+"F0.wireOp",EDGE,"E2"),sQuery(id+"F0.wireOp",EDGE,"E3"),sQuery(id+"F0.wireOp",EDGE,"E4"),sQuery(id+"F0.wireOp",EDGE,"E5"),sQuery(id+"F0.wireOp",EDGE,"E6"),sQuery(id+"F0.wireOp",EDGE,"E7"),sQuery(id+"F0.wireOp",EDGE,"E8"),sQuery(id+"F0.wireOp",EDGE,"E9"),sQuery(id+"F0.wireOp",EDGE,"E10"),sQuery(id+"F0.wireOp",EDGE,"E11"),sQuery(id+"F0.wireOp",EDGE,"E12"),sQuery(id+"F0.wireOp",EDGE,"E13"),sQuery(id+"F0.wireOp",EDGE,"E14"),sQuery(id+"F0.wireOp",EDGE,"E15"),sQuery(id+"F0.wireOp",EDGE,"E16"),sQuery(id+"F0.wireOp",EDGE,"E17"),sQuery(id+"F0.wireOp",EDGE,"E18"),sQuery(id+"F0.wireOp",EDGE,"E19"),sQuery(id+"F0.wireOp",EDGE,"E20"),sQuery(id+"F0.wireOp",EDGE,"E21"),sQuery(id+"F0.wireOp",EDGE,"E22"),sQuery(id+"F0.wireOp",EDGE,"E23"),sQuery(id+"F0.wireOp",EDGE,"E24"),sQuery(id+"F0.wireOp",EDGE,"E25"),sQuery(id+"F0.wireOp",EDGE,"E26"),sQuery(id+"F0.wireOp",EDGE,"E27"),sQuery(id+"F0.wireOp",EDGE,"E28"),sQuery(id+"F0.wireOp",EDGE,"E29"),sQuery(id+"F0.wireOp",EDGE,"E30"),sQuery(id+"F0.wireOp",EDGE,"E31"),sQuery(id+"F0.wireOp",EDGE,"E32"),sQuery(id+"F0.wireOp",EDGE,"E33"),sQuery(id+"F0.wireOp",EDGE,"E34"),sQuery(id+"F0.wireOp",EDGE,"E35"),sQuery(id+"F0.wireOp",EDGE,"E36"),sQuery(id+"F0.wireOp",EDGE,"E37"),sQuery(id+"F0.wireOp",EDGE,"E38"),sQuery(id+"F0.wireOp",EDGE,"E39"),sQuery(id+"F0.wireOp",EDGE,"E40"),sQuery(id+"F0.wireOp",EDGE,"E41"),sQuery(id+"F0.wireOp",EDGE,"E42"),sQuery(id+"F0.wireOp",EDGE,"E43"),sQuery(id+"F0.wireOp",EDGE,"E44"),sQuery(id+"F0.wireOp",EDGE,"E45"),sQuery(id+"F0.wireOp",EDGE,"E46"),sQuery(id+"F0.wireOp",EDGE,"E47"),sQuery(id+"F0.wireOp",EDGE,"E48"),sQuery(id+"F0.wireOp",EDGE,"E49"),sQuery(id+"F0.wireOp",EDGE,"E50"),sQuery(id+"F0.wireOp",EDGE,"E51"),sQuery(id+"F0.wireOp",EDGE,"E52"),sQuery(id+"F0.wireOp",EDGE,"E53"),sQuery(id+"F0.wireOp",EDGE,"E54"),sQuery(id+"F0.wireOp",EDGE,"E55"),sQuery(id+"F0.wireOp",EDGE,"E56"),sQuery(id+"F0.wireOp",EDGE,"E57"),sQuery(id+"F0.wireOp",EDGE,"E58"),sQuery(id+"F0.wireOp",EDGE,"E59"),sQuery(id+"F0.wireOp",EDGE,"E60"),sQuery(id+"F0.wireOp",EDGE,"E61"),sQuery(id+"F0.wireOp",EDGE,"E62"),sQuery(id+"F0.wireOp",EDGE,"E63"),sQuery(id+"F0.wireOp",EDGE,"E64"),sQuery(id+"F0.wireOp",EDGE,"E65"),sQuery(id+"F0.wireOp",EDGE,"E66"),sQuery(id+"F0.wireOp",EDGE,"E67"),sQuery(id+"F0.wireOp",EDGE,"E68"),sQuery(id+"F0.wireOp",EDGE,"E69"),sQuery(id+"F0.wireOp",EDGE,"E70"),sQuery(id+"F0.wireOp",EDGE,"E71"),sQuery(id+"F0.wireOp",EDGE,"E72"),sQuery(id+"F0.wireOp",EDGE,"E73"),sQuery(id+"F0.wireOp",EDGE,"E74"),sQuery(id+"F0.wireOp",EDGE,"E75"),sQuery(id+"F0.wireOp",EDGE,"E76"),sQuery(id+"F0.wireOp",EDGE,"E77"),sQuery(id+"F0.wireOp",EDGE,"E78"),sQuery(id+"F0.wireOp",EDGE,"E79"),sQuery(id+"F0.wireOp",EDGE,"E80"),sQuery(id+"F0.wireOp",EDGE,"E81"),sQuery(id+"F0.wireOp",EDGE,"E82"),sQuery(id+"F0.wireOp",EDGE,"E83"),sQuery(id+"F0.wireOp",EDGE,"E84"),sQuery(id+"F0.wireOp",EDGE,"E85"),sQuery(id+"F0.wireOp",EDGE,"E86"),sQuery(id+"F0.wireOp",EDGE,"E87"),sQuery(id+"F0.wireOp",EDGE,"E88"),sQuery(id+"F0.wireOp",EDGE,"E89"),sQuery(id+"F0.wireOp",EDGE,"E90")])]});
            transform(context, id + "F6", {"entities" : qUnion([Q0]), "transformType" : TransformType.TRANSLATION_3D, "dx" : 1.04 * mm, "dy" : -0.35 * mm, "dz" : 0 * mm, "makeCopy" : false});
        }
        {
            var Q0;
            Q0=makeQuery(id+"F1.opExtrude","SWEPT_BODY",BODY,{"disambiguationData":[OSD([sQuery(id+"F0.wireOp",EDGE,"E154"),sQuery(id+"F0.wireOp",EDGE,"E155"),sQuery(id+"F0.wireOp",EDGE,"E156"),sQuery(id+"F0.wireOp",EDGE,"E157"),sQuery(id+"F0.wireOp",EDGE,"E158"),sQuery(id+"F0.wireOp",EDGE,"E159"),sQuery(id+"F0.wireOp",EDGE,"E160"),sQuery(id+"F0.wireOp",EDGE,"E161"),sQuery(id+"F0.wireOp",EDGE,"E162"),sQuery(id+"F0.wireOp",EDGE,"E163"),sQuery(id+"F0.wireOp",EDGE,"E164"),sQuery(id+"F0.wireOp",EDGE,"E165"),sQuery(id+"F0.wireOp",EDGE,"E166"),sQuery(id+"F0.wireOp",EDGE,"E167"),sQuery(id+"F0.wireOp",EDGE,"E168"),sQuery(id+"F0.wireOp",EDGE,"E169"),sQuery(id+"F0.wireOp",EDGE,"E170"),sQuery(id+"F0.wireOp",EDGE,"E171"),sQuery(id+"F0.wireOp",EDGE,"E172"),sQuery(id+"F0.wireOp",EDGE,"E173"),sQuery(id+"F0.wireOp",EDGE,"E174"),sQuery(id+"F0.wireOp",EDGE,"E175"),sQuery(id+"F0.wireOp",EDGE,"E176"),sQuery(id+"F0.wireOp",EDGE,"E177"),sQuery(id+"F0.wireOp",EDGE,"E178"),sQuery(id+"F0.wireOp",EDGE,"E179"),sQuery(id+"F0.wireOp",EDGE,"E180"),sQuery(id+"F0.wireOp",EDGE,"E181"),sQuery(id+"F0.wireOp",EDGE,"E182"),sQuery(id+"F0.wireOp",EDGE,"E183"),sQuery(id+"F0.wireOp",EDGE,"E184"),sQuery(id+"F0.wireOp",EDGE,"E185"),sQuery(id+"F0.wireOp",EDGE,"E186"),sQuery(id+"F0.wireOp",EDGE,"E187"),sQuery(id+"F0.wireOp",EDGE,"E188"),sQuery(id+"F0.wireOp",EDGE,"E189"),sQuery(id+"F0.wireOp",EDGE,"E190"),sQuery(id+"F0.wireOp",EDGE,"E191"),sQuery(id+"F0.wireOp",EDGE,"E192"),sQuery(id+"F0.wireOp",EDGE,"E193"),sQuery(id+"F0.wireOp",EDGE,"E194"),sQuery(id+"F0.wireOp",EDGE,"E195"),sQuery(id+"F0.wireOp",EDGE,"E196"),sQuery(id+"F0.wireOp",EDGE,"E197"),sQuery(id+"F0.wireOp",EDGE,"E198"),sQuery(id+"F0.wireOp",EDGE,"E199"),sQuery(id+"F0.wireOp",EDGE,"E200"),sQuery(id+"F0.wireOp",EDGE,"E201"),sQuery(id+"F0.wireOp",EDGE,"E202"),sQuery(id+"F0.wireOp",EDGE,"E203"),sQuery(id+"F0.wireOp",EDGE,"E204"),sQuery(id+"F0.wireOp",EDGE,"E205"),sQuery(id+"F0.wireOp",EDGE,"E206"),sQuery(id+"F0.wireOp",EDGE,"E207"),sQuery(id+"F0.wireOp",EDGE,"E208"),sQuery(id+"F0.wireOp",EDGE,"E209"),sQuery(id+"F0.wireOp",EDGE,"E210"),sQuery(id+"F0.wireOp",EDGE,"E211"),sQuery(id+"F0.wireOp",EDGE,"E212"),sQuery(id+"F0.wireOp",EDGE,"E213"),sQuery(id+"F0.wireOp",EDGE,"E214"),sQuery(id+"F0.wireOp",EDGE,"E215"),sQuery(id+"F0.wireOp",EDGE,"E216"),sQuery(id+"F0.wireOp",EDGE,"E217"),sQuery(id+"F0.wireOp",EDGE,"E218"),sQuery(id+"F0.wireOp",EDGE,"E219"),sQuery(id+"F0.wireOp",EDGE,"E220")])]});
            transform(context, id + "F7", {"entities" : qUnion([Q0]), "transformType" : TransformType.TRANSLATION_3D, "dx" : -2.2 * mm, "dy" : -0.51 * mm, "dz" : 0 * mm, "makeCopy" : false});
        }
        {
            var Q0;
            Q0=makeQuery(id+"F1.opExtrude","SWEPT_BODY",BODY,{"disambiguationData":[OSD([sQuery(id+"F0.wireOp",EDGE,"E0"),sQuery(id+"F0.wireOp",EDGE,"E1"),sQuery(id+"F0.wireOp",EDGE,"E2"),sQuery(id+"F0.wireOp",EDGE,"E3"),sQuery(id+"F0.wireOp",EDGE,"E4"),sQuery(id+"F0.wireOp",EDGE,"E5"),sQuery(id+"F0.wireOp",EDGE,"E6"),sQuery(id+"F0.wireOp",EDGE,"E7"),sQuery(id+"F0.wireOp",EDGE,"E8"),sQuery(id+"F0.wireOp",EDGE,"E9"),sQuery(id+"F0.wireOp",EDGE,"E10"),sQuery(id+"F0.wireOp",EDGE,"E11"),sQuery(id+"F0.wireOp",EDGE,"E12"),sQuery(id+"F0.wireOp",EDGE,"E13"),sQuery(id+"F0.wireOp",EDGE,"E14"),sQuery(id+"F0.wireOp",EDGE,"E15"),sQuery(id+"F0.wireOp",EDGE,"E16"),sQuery(id+"F0.wireOp",EDGE,"E17"),sQuery(id+"F0.wireOp",EDGE,"E18"),sQuery(id+"F0.wireOp",EDGE,"E19"),sQuery(id+"F0.wireOp",EDGE,"E20"),sQuery(id+"F0.wireOp",EDGE,"E21"),sQuery(id+"F0.wireOp",EDGE,"E22"),sQuery(id+"F0.wireOp",EDGE,"E23"),sQuery(id+"F0.wireOp",EDGE,"E24"),sQuery(id+"F0.wireOp",EDGE,"E25"),sQuery(id+"F0.wireOp",EDGE,"E26"),sQuery(id+"F0.wireOp",EDGE,"E27"),sQuery(id+"F0.wireOp",EDGE,"E28"),sQuery(id+"F0.wireOp",EDGE,"E29"),sQuery(id+"F0.wireOp",EDGE,"E30"),sQuery(id+"F0.wireOp",EDGE,"E31"),sQuery(id+"F0.wireOp",EDGE,"E32"),sQuery(id+"F0.wireOp",EDGE,"E33"),sQuery(id+"F0.wireOp",EDGE,"E34"),sQuery(id+"F0.wireOp",EDGE,"E35"),sQuery(id+"F0.wireOp",EDGE,"E36"),sQuery(id+"F0.wireOp",EDGE,"E37"),sQuery(id+"F0.wireOp",EDGE,"E38"),sQuery(id+"F0.wireOp",EDGE,"E39"),sQuery(id+"F0.wireOp",EDGE,"E40"),sQuery(id+"F0.wireOp",EDGE,"E41"),sQuery(id+"F0.wireOp",EDGE,"E42"),sQuery(id+"F0.wireOp",EDGE,"E43"),sQuery(id+"F0.wireOp",EDGE,"E44"),sQuery(id+"F0.wireOp",EDGE,"E45"),sQuery(id+"F0.wireOp",EDGE,"E46"),sQuery(id+"F0.wireOp",EDGE,"E47"),sQuery(id+"F0.wireOp",EDGE,"E48"),sQuery(id+"F0.wireOp",EDGE,"E49"),sQuery(id+"F0.wireOp",EDGE,"E50"),sQuery(id+"F0.wireOp",EDGE,"E51"),sQuery(id+"F0.wireOp",EDGE,"E52"),sQuery(id+"F0.wireOp",EDGE,"E53"),sQuery(id+"F0.wireOp",EDGE,"E54"),sQuery(id+"F0.wireOp",EDGE,"E55"),sQuery(id+"F0.wireOp",EDGE,"E56"),sQuery(id+"F0.wireOp",EDGE,"E57"),sQuery(id+"F0.wireOp",EDGE,"E58"),sQuery(id+"F0.wireOp",EDGE,"E59"),sQuery(id+"F0.wireOp",EDGE,"E60"),sQuery(id+"F0.wireOp",EDGE,"E61"),sQuery(id+"F0.wireOp",EDGE,"E62"),sQuery(id+"F0.wireOp",EDGE,"E63"),sQuery(id+"F0.wireOp",EDGE,"E64"),sQuery(id+"F0.wireOp",EDGE,"E65"),sQuery(id+"F0.wireOp",EDGE,"E66"),sQuery(id+"F0.wireOp",EDGE,"E67"),sQuery(id+"F0.wireOp",EDGE,"E68"),sQuery(id+"F0.wireOp",EDGE,"E69"),sQuery(id+"F0.wireOp",EDGE,"E70"),sQuery(id+"F0.wireOp",EDGE,"E71"),sQuery(id+"F0.wireOp",EDGE,"E72"),sQuery(id+"F0.wireOp",EDGE,"E73"),sQuery(id+"F0.wireOp",EDGE,"E74"),sQuery(id+"F0.wireOp",EDGE,"E75"),sQuery(id+"F0.wireOp",EDGE,"E76"),sQuery(id+"F0.wireOp",EDGE,"E77"),sQuery(id+"F0.wireOp",EDGE,"E78"),sQuery(id+"F0.wireOp",EDGE,"E79"),sQuery(id+"F0.wireOp",EDGE,"E80"),sQuery(id+"F0.wireOp",EDGE,"E81"),sQuery(id+"F0.wireOp",EDGE,"E82"),sQuery(id+"F0.wireOp",EDGE,"E83"),sQuery(id+"F0.wireOp",EDGE,"E84"),sQuery(id+"F0.wireOp",EDGE,"E85"),sQuery(id+"F0.wireOp",EDGE,"E86"),sQuery(id+"F0.wireOp",EDGE,"E87"),sQuery(id+"F0.wireOp",EDGE,"E88"),sQuery(id+"F0.wireOp",EDGE,"E89"),sQuery(id+"F0.wireOp",EDGE,"E90")])]});
            var Q1;
            Q1=qCreatedBy(makeId("Origin.pointOp"),VERTEX);
            transform(context, id + "F8", {"entities" : qUnion([Q0]), "transformType" : TransformType.SCALE_UNIFORMLY, "scale" : 1.6, "scalePoint" : qUnion([Q1]), "makeCopy" : false});
        }
        {
            var Q0;
            Q0=makeQuery(id+"F1.opExtrude","SWEPT_BODY",BODY,{"disambiguationData":[OSD([sQuery(id+"F0.wireOp",EDGE,"E0"),sQuery(id+"F0.wireOp",EDGE,"E1"),sQuery(id+"F0.wireOp",EDGE,"E2"),sQuery(id+"F0.wireOp",EDGE,"E3"),sQuery(id+"F0.wireOp",EDGE,"E4"),sQuery(id+"F0.wireOp",EDGE,"E5"),sQuery(id+"F0.wireOp",EDGE,"E6"),sQuery(id+"F0.wireOp",EDGE,"E7"),sQuery(id+"F0.wireOp",EDGE,"E8"),sQuery(id+"F0.wireOp",EDGE,"E9"),sQuery(id+"F0.wireOp",EDGE,"E10"),sQuery(id+"F0.wireOp",EDGE,"E11"),sQuery(id+"F0.wireOp",EDGE,"E12"),sQuery(id+"F0.wireOp",EDGE,"E13"),sQuery(id+"F0.wireOp",EDGE,"E14"),sQuery(id+"F0.wireOp",EDGE,"E15"),sQuery(id+"F0.wireOp",EDGE,"E16"),sQuery(id+"F0.wireOp",EDGE,"E17"),sQuery(id+"F0.wireOp",EDGE,"E18"),sQuery(id+"F0.wireOp",EDGE,"E19"),sQuery(id+"F0.wireOp",EDGE,"E20"),sQuery(id+"F0.wireOp",EDGE,"E21"),sQuery(id+"F0.wireOp",EDGE,"E22"),sQuery(id+"F0.wireOp",EDGE,"E23"),sQuery(id+"F0.wireOp",EDGE,"E24"),sQuery(id+"F0.wireOp",EDGE,"E25"),sQuery(id+"F0.wireOp",EDGE,"E26"),sQuery(id+"F0.wireOp",EDGE,"E27"),sQuery(id+"F0.wireOp",EDGE,"E28"),sQuery(id+"F0.wireOp",EDGE,"E29"),sQuery(id+"F0.wireOp",EDGE,"E30"),sQuery(id+"F0.wireOp",EDGE,"E31"),sQuery(id+"F0.wireOp",EDGE,"E32"),sQuery(id+"F0.wireOp",EDGE,"E33"),sQuery(id+"F0.wireOp",EDGE,"E34"),sQuery(id+"F0.wireOp",EDGE,"E35"),sQuery(id+"F0.wireOp",EDGE,"E36"),sQuery(id+"F0.wireOp",EDGE,"E37"),sQuery(id+"F0.wireOp",EDGE,"E38"),sQuery(id+"F0.wireOp",EDGE,"E39"),sQuery(id+"F0.wireOp",EDGE,"E40"),sQuery(id+"F0.wireOp",EDGE,"E41"),sQuery(id+"F0.wireOp",EDGE,"E42"),sQuery(id+"F0.wireOp",EDGE,"E43"),sQuery(id+"F0.wireOp",EDGE,"E44"),sQuery(id+"F0.wireOp",EDGE,"E45"),sQuery(id+"F0.wireOp",EDGE,"E46"),sQuery(id+"F0.wireOp",EDGE,"E47"),sQuery(id+"F0.wireOp",EDGE,"E48"),sQuery(id+"F0.wireOp",EDGE,"E49"),sQuery(id+"F0.wireOp",EDGE,"E50"),sQuery(id+"F0.wireOp",EDGE,"E51"),sQuery(id+"F0.wireOp",EDGE,"E52"),sQuery(id+"F0.wireOp",EDGE,"E53"),sQuery(id+"F0.wireOp",EDGE,"E54"),sQuery(id+"F0.wireOp",EDGE,"E55"),sQuery(id+"F0.wireOp",EDGE,"E56"),sQuery(id+"F0.wireOp",EDGE,"E57"),sQuery(id+"F0.wireOp",EDGE,"E58"),sQuery(id+"F0.wireOp",EDGE,"E59"),sQuery(id+"F0.wireOp",EDGE,"E60"),sQuery(id+"F0.wireOp",EDGE,"E61"),sQuery(id+"F0.wireOp",EDGE,"E62"),sQuery(id+"F0.wireOp",EDGE,"E63"),sQuery(id+"F0.wireOp",EDGE,"E64"),sQuery(id+"F0.wireOp",EDGE,"E65"),sQuery(id+"F0.wireOp",EDGE,"E66"),sQuery(id+"F0.wireOp",EDGE,"E67"),sQuery(id+"F0.wireOp",EDGE,"E68"),sQuery(id+"F0.wireOp",EDGE,"E69"),sQuery(id+"F0.wireOp",EDGE,"E70"),sQuery(id+"F0.wireOp",EDGE,"E71"),sQuery(id+"F0.wireOp",EDGE,"E72"),sQuery(id+"F0.wireOp",EDGE,"E73"),sQuery(id+"F0.wireOp",EDGE,"E74"),sQuery(id+"F0.wireOp",EDGE,"E75"),sQuery(id+"F0.wireOp",EDGE,"E76"),sQuery(id+"F0.wireOp",EDGE,"E77"),sQuery(id+"F0.wireOp",EDGE,"E78"),sQuery(id+"F0.wireOp",EDGE,"E79"),sQuery(id+"F0.wireOp",EDGE,"E80"),sQuery(id+"F0.wireOp",EDGE,"E81"),sQuery(id+"F0.wireOp",EDGE,"E82"),sQuery(id+"F0.wireOp",EDGE,"E83"),sQuery(id+"F0.wireOp",EDGE,"E84"),sQuery(id+"F0.wireOp",EDGE,"E85"),sQuery(id+"F0.wireOp",EDGE,"E86"),sQuery(id+"F0.wireOp",EDGE,"E87"),sQuery(id+"F0.wireOp",EDGE,"E88"),sQuery(id+"F0.wireOp",EDGE,"E89"),sQuery(id+"F0.wireOp",EDGE,"E90")])]});
            transform(context, id + "F9", {"entities" : qUnion([Q0]), "transformType" : TransformType.TRANSLATION_3D, "dx" : 3.77 * mm, "dy" : 0 * mm, "dz" : 0 * mm, "makeCopy" : false});
        }
        {
            var Q0;
            Q0=makeQuery(id+"F1.opExtrude","SWEPT_BODY",BODY,{"disambiguationData":[OSD([sQuery(id+"F0.wireOp",EDGE,"E0"),sQuery(id+"F0.wireOp",EDGE,"E1"),sQuery(id+"F0.wireOp",EDGE,"E2"),sQuery(id+"F0.wireOp",EDGE,"E3"),sQuery(id+"F0.wireOp",EDGE,"E4"),sQuery(id+"F0.wireOp",EDGE,"E5"),sQuery(id+"F0.wireOp",EDGE,"E6"),sQuery(id+"F0.wireOp",EDGE,"E7"),sQuery(id+"F0.wireOp",EDGE,"E8"),sQuery(id+"F0.wireOp",EDGE,"E9"),sQuery(id+"F0.wireOp",EDGE,"E10"),sQuery(id+"F0.wireOp",EDGE,"E11"),sQuery(id+"F0.wireOp",EDGE,"E12"),sQuery(id+"F0.wireOp",EDGE,"E13"),sQuery(id+"F0.wireOp",EDGE,"E14"),sQuery(id+"F0.wireOp",EDGE,"E15"),sQuery(id+"F0.wireOp",EDGE,"E16"),sQuery(id+"F0.wireOp",EDGE,"E17"),sQuery(id+"F0.wireOp",EDGE,"E18"),sQuery(id+"F0.wireOp",EDGE,"E19"),sQuery(id+"F0.wireOp",EDGE,"E20"),sQuery(id+"F0.wireOp",EDGE,"E21"),sQuery(id+"F0.wireOp",EDGE,"E22"),sQuery(id+"F0.wireOp",EDGE,"E23"),sQuery(id+"F0.wireOp",EDGE,"E24"),sQuery(id+"F0.wireOp",EDGE,"E25"),sQuery(id+"F0.wireOp",EDGE,"E26"),sQuery(id+"F0.wireOp",EDGE,"E27"),sQuery(id+"F0.wireOp",EDGE,"E28"),sQuery(id+"F0.wireOp",EDGE,"E29"),sQuery(id+"F0.wireOp",EDGE,"E30"),sQuery(id+"F0.wireOp",EDGE,"E31"),sQuery(id+"F0.wireOp",EDGE,"E32"),sQuery(id+"F0.wireOp",EDGE,"E33"),sQuery(id+"F0.wireOp",EDGE,"E34"),sQuery(id+"F0.wireOp",EDGE,"E35"),sQuery(id+"F0.wireOp",EDGE,"E36"),sQuery(id+"F0.wireOp",EDGE,"E37"),sQuery(id+"F0.wireOp",EDGE,"E38"),sQuery(id+"F0.wireOp",EDGE,"E39"),sQuery(id+"F0.wireOp",EDGE,"E40"),sQuery(id+"F0.wireOp",EDGE,"E41"),sQuery(id+"F0.wireOp",EDGE,"E42"),sQuery(id+"F0.wireOp",EDGE,"E43"),sQuery(id+"F0.wireOp",EDGE,"E44"),sQuery(id+"F0.wireOp",EDGE,"E45"),sQuery(id+"F0.wireOp",EDGE,"E46"),sQuery(id+"F0.wireOp",EDGE,"E47"),sQuery(id+"F0.wireOp",EDGE,"E48"),sQuery(id+"F0.wireOp",EDGE,"E49"),sQuery(id+"F0.wireOp",EDGE,"E50"),sQuery(id+"F0.wireOp",EDGE,"E51"),sQuery(id+"F0.wireOp",EDGE,"E52"),sQuery(id+"F0.wireOp",EDGE,"E53"),sQuery(id+"F0.wireOp",EDGE,"E54"),sQuery(id+"F0.wireOp",EDGE,"E55"),sQuery(id+"F0.wireOp",EDGE,"E56"),sQuery(id+"F0.wireOp",EDGE,"E57"),sQuery(id+"F0.wireOp",EDGE,"E58"),sQuery(id+"F0.wireOp",EDGE,"E59"),sQuery(id+"F0.wireOp",EDGE,"E60"),sQuery(id+"F0.wireOp",EDGE,"E61"),sQuery(id+"F0.wireOp",EDGE,"E62"),sQuery(id+"F0.wireOp",EDGE,"E63"),sQuery(id+"F0.wireOp",EDGE,"E64"),sQuery(id+"F0.wireOp",EDGE,"E65"),sQuery(id+"F0.wireOp",EDGE,"E66"),sQuery(id+"F0.wireOp",EDGE,"E67"),sQuery(id+"F0.wireOp",EDGE,"E68"),sQuery(id+"F0.wireOp",EDGE,"E69"),sQuery(id+"F0.wireOp",EDGE,"E70"),sQuery(id+"F0.wireOp",EDGE,"E71"),sQuery(id+"F0.wireOp",EDGE,"E72"),sQuery(id+"F0.wireOp",EDGE,"E73"),sQuery(id+"F0.wireOp",EDGE,"E74"),sQuery(id+"F0.wireOp",EDGE,"E75"),sQuery(id+"F0.wireOp",EDGE,"E76"),sQuery(id+"F0.wireOp",EDGE,"E77"),sQuery(id+"F0.wireOp",EDGE,"E78"),sQuery(id+"F0.wireOp",EDGE,"E79"),sQuery(id+"F0.wireOp",EDGE,"E80"),sQuery(id+"F0.wireOp",EDGE,"E81"),sQuery(id+"F0.wireOp",EDGE,"E82"),sQuery(id+"F0.wireOp",EDGE,"E83"),sQuery(id+"F0.wireOp",EDGE,"E84"),sQuery(id+"F0.wireOp",EDGE,"E85"),sQuery(id+"F0.wireOp",EDGE,"E86"),sQuery(id+"F0.wireOp",EDGE,"E87"),sQuery(id+"F0.wireOp",EDGE,"E88"),sQuery(id+"F0.wireOp",EDGE,"E89"),sQuery(id+"F0.wireOp",EDGE,"E90")])]});
            transform(context, id + "F10", {"entities" : qUnion([Q0]), "transformType" : TransformType.TRANSLATION_3D, "dx" : -4.15 * mm, "dy" : 2.47 * mm, "dz" : 0 * mm, "makeCopy" : false});
        }
        {
            var Q0;
            Q0=qCreatedBy(makeId("Top.planeOp"),FACE);
            var sketch = newSketch(context, id + "F11", { "sketchPlane" : qUnion([Q0])});
            skEllipse(sketch, "E221", {"center": v(0, 0) * mm, "majorRadius": 20.85 * mm, "minorRadius": 10.42 * mm, "majorAxis": v(-1, 0)});
            skFitSpline(sketch, "E222.0", {"points": [v(-22.02, 1.27) * mm, v(-22.15, 0) * mm, v(-22.02, -1.27) * mm, v(-21.65, -2.5) * mm, v(-21.06, -3.68) * mm, v(-20.26, -4.8) * mm, v(-19.28, -5.84) * mm, v(-17.72, -7.13) * mm, v(-15.4, -8.54) * mm, v(-12.62, -9.68) * mm, v(-10.16, -10.42) * mm, v(-7.6, -11.02) * mm, v(-4.9, -11.43) * mm, v(-2.12, -11.64) * mm, v(0, -11.7) * mm, v(2.12, -11.64) * mm, v(4.9, -11.43) * mm, v(7.6, -11.02) * mm, v(10.16, -10.42) * mm, v(12.62, -9.68) * mm, v(15.4, -8.54) * mm, v(17.72, -7.13) * mm, v(19.28, -5.84) * mm, v(20.26, -4.8) * mm, v(21.06, -3.68) * mm, v(21.65, -2.5) * mm, v(22.02, -1.27) * mm, v(22.15, 0) * mm, v(22.02, 1.27) * mm, v(21.65, 2.5) * mm, v(21.06, 3.68) * mm, v(20.26, 4.8) * mm, v(19.28, 5.84) * mm, v(17.72, 7.13) * mm, v(15.4, 8.54) * mm, v(12.62, 9.68) * mm, v(10.16, 10.42) * mm, v(7.6, 11.02) * mm, v(4.9, 11.43) * mm, v(2.12, 11.64) * mm, v(0, 11.7) * mm, v(-2.12, 11.64) * mm, v(-4.9, 11.43) * mm, v(-7.6, 11.02) * mm, v(-10.16, 10.42) * mm, v(-12.62, 9.68) * mm, v(-15.4, 8.54) * mm, v(-17.72, 7.13) * mm, v(-19.28, 5.84) * mm, v(-20.26, 4.8) * mm, v(-21.06, 3.68) * mm, v(-21.65, 2.5) * mm, v(-22.02, 1.27) * mm, v(-22.15, 0) * mm, v(-22.02, -1.27) * mm, v(-22.02, 1.27) * mm]});
            skSolve(sketch);
        }
        {
            var Q0;
            Q0 = qSketchRegion(id + "F11", true);
            extrude(context, id + "F12", {"entities" : qUnion([Q0]), "depth" : 5 * mm});
        }
        {
            var Q0;
            Q0=makeQuery(id+"F1.opExtrude","SWEPT_BODY",BODY,{"disambiguationData":[OSD([sQuery(id+"F0.wireOp",EDGE,"E0"),sQuery(id+"F0.wireOp",EDGE,"E1"),sQuery(id+"F0.wireOp",EDGE,"E2"),sQuery(id+"F0.wireOp",EDGE,"E3"),sQuery(id+"F0.wireOp",EDGE,"E4"),sQuery(id+"F0.wireOp",EDGE,"E5"),sQuery(id+"F0.wireOp",EDGE,"E6"),sQuery(id+"F0.wireOp",EDGE,"E7"),sQuery(id+"F0.wireOp",EDGE,"E8"),sQuery(id+"F0.wireOp",EDGE,"E9"),sQuery(id+"F0.wireOp",EDGE,"E10"),sQuery(id+"F0.wireOp",EDGE,"E11"),sQuery(id+"F0.wireOp",EDGE,"E12"),sQuery(id+"F0.wireOp",EDGE,"E13"),sQuery(id+"F0.wireOp",EDGE,"E14"),sQuery(id+"F0.wireOp",EDGE,"E15"),sQuery(id+"F0.wireOp",EDGE,"E16"),sQuery(id+"F0.wireOp",EDGE,"E17"),sQuery(id+"F0.wireOp",EDGE,"E18"),sQuery(id+"F0.wireOp",EDGE,"E19"),sQuery(id+"F0.wireOp",EDGE,"E20"),sQuery(id+"F0.wireOp",EDGE,"E21"),sQuery(id+"F0.wireOp",EDGE,"E22"),sQuery(id+"F0.wireOp",EDGE,"E23"),sQuery(id+"F0.wireOp",EDGE,"E24"),sQuery(id+"F0.wireOp",EDGE,"E25"),sQuery(id+"F0.wireOp",EDGE,"E26"),sQuery(id+"F0.wireOp",EDGE,"E27"),sQuery(id+"F0.wireOp",EDGE,"E28"),sQuery(id+"F0.wireOp",EDGE,"E29"),sQuery(id+"F0.wireOp",EDGE,"E30"),sQuery(id+"F0.wireOp",EDGE,"E31"),sQuery(id+"F0.wireOp",EDGE,"E32"),sQuery(id+"F0.wireOp",EDGE,"E33"),sQuery(id+"F0.wireOp",EDGE,"E34"),sQuery(id+"F0.wireOp",EDGE,"E35"),sQuery(id+"F0.wireOp",EDGE,"E36"),sQuery(id+"F0.wireOp",EDGE,"E37"),sQuery(id+"F0.wireOp",EDGE,"E38"),sQuery(id+"F0.wireOp",EDGE,"E39"),sQuery(id+"F0.wireOp",EDGE,"E40"),sQuery(id+"F0.wireOp",EDGE,"E41"),sQuery(id+"F0.wireOp",EDGE,"E42"),sQuery(id+"F0.wireOp",EDGE,"E43"),sQuery(id+"F0.wireOp",EDGE,"E44"),sQuery(id+"F0.wireOp",EDGE,"E45"),sQuery(id+"F0.wireOp",EDGE,"E46"),sQuery(id+"F0.wireOp",EDGE,"E47"),sQuery(id+"F0.wireOp",EDGE,"E48"),sQuery(id+"F0.wireOp",EDGE,"E49"),sQuery(id+"F0.wireOp",EDGE,"E50"),sQuery(id+"F0.wireOp",EDGE,"E51"),sQuery(id+"F0.wireOp",EDGE,"E52"),sQuery(id+"F0.wireOp",EDGE,"E53"),sQuery(id+"F0.wireOp",EDGE,"E54"),sQuery(id+"F0.wireOp",EDGE,"E55"),sQuery(id+"F0.wireOp",EDGE,"E56"),sQuery(id+"F0.wireOp",EDGE,"E57"),sQuery(id+"F0.wireOp",EDGE,"E58"),sQuery(id+"F0.wireOp",EDGE,"E59"),sQuery(id+"F0.wireOp",EDGE,"E60"),sQuery(id+"F0.wireOp",EDGE,"E61"),sQuery(id+"F0.wireOp",EDGE,"E62"),sQuery(id+"F0.wireOp",EDGE,"E63"),sQuery(id+"F0.wireOp",EDGE,"E64"),sQuery(id+"F0.wireOp",EDGE,"E65"),sQuery(id+"F0.wireOp",EDGE,"E66"),sQuery(id+"F0.wireOp",EDGE,"E67"),sQuery(id+"F0.wireOp",EDGE,"E68"),sQuery(id+"F0.wireOp",EDGE,"E69"),sQuery(id+"F0.wireOp",EDGE,"E70"),sQuery(id+"F0.wireOp",EDGE,"E71"),sQuery(id+"F0.wireOp",EDGE,"E72"),sQuery(id+"F0.wireOp",EDGE,"E73"),sQuery(id+"F0.wireOp",EDGE,"E74"),sQuery(id+"F0.wireOp",EDGE,"E75"),sQuery(id+"F0.wireOp",EDGE,"E76"),sQuery(id+"F0.wireOp",EDGE,"E77"),sQuery(id+"F0.wireOp",EDGE,"E78"),sQuery(id+"F0.wireOp",EDGE,"E79"),sQuery(id+"F0.wireOp",EDGE,"E80"),sQuery(id+"F0.wireOp",EDGE,"E81"),sQuery(id+"F0.wireOp",EDGE,"E82"),sQuery(id+"F0.wireOp",EDGE,"E83"),sQuery(id+"F0.wireOp",EDGE,"E84"),sQuery(id+"F0.wireOp",EDGE,"E85"),sQuery(id+"F0.wireOp",EDGE,"E86"),sQuery(id+"F0.wireOp",EDGE,"E87"),sQuery(id+"F0.wireOp",EDGE,"E88"),sQuery(id+"F0.wireOp",EDGE,"E89"),sQuery(id+"F0.wireOp",EDGE,"E90")])]});
            var Q1;
            Q1=makeQuery(id+"F12.opExtrude","SWEPT_BODY",BODY,{"disambiguationData":[OSD([sQuery(id+"F11.wireOp",EDGE,"E221"),sQuery(id+"F11.wireOp",EDGE,"E222.0")])]});
            booleanBodies(context, id + "F13", {"operationType" : BooleanOperationType.UNION, "tools" : qUnion([Q0, Q1])});
        }
        {
            var Q0;
            Q0=makeQuery(id+"F1.opExtrude","SWEPT_BODY",BODY,{"disambiguationData":[OSD([sQuery(id+"F0.wireOp",EDGE,"E0"),sQuery(id+"F0.wireOp",EDGE,"E1"),sQuery(id+"F0.wireOp",EDGE,"E2"),sQuery(id+"F0.wireOp",EDGE,"E3"),sQuery(id+"F0.wireOp",EDGE,"E4"),sQuery(id+"F0.wireOp",EDGE,"E5"),sQuery(id+"F0.wireOp",EDGE,"E6"),sQuery(id+"F0.wireOp",EDGE,"E7"),sQuery(id+"F0.wireOp",EDGE,"E8"),sQuery(id+"F0.wireOp",EDGE,"E9"),sQuery(id+"F0.wireOp",EDGE,"E10"),sQuery(id+"F0.wireOp",EDGE,"E11"),sQuery(id+"F0.wireOp",EDGE,"E12"),sQuery(id+"F0.wireOp",EDGE,"E13"),sQuery(id+"F0.wireOp",EDGE,"E14"),sQuery(id+"F0.wireOp",EDGE,"E15"),sQuery(id+"F0.wireOp",EDGE,"E16"),sQuery(id+"F0.wireOp",EDGE,"E17"),sQuery(id+"F0.wireOp",EDGE,"E18"),sQuery(id+"F0.wireOp",EDGE,"E19"),sQuery(id+"F0.wireOp",EDGE,"E20"),sQuery(id+"F0.wireOp",EDGE,"E21"),sQuery(id+"F0.wireOp",EDGE,"E22"),sQuery(id+"F0.wireOp",EDGE,"E23"),sQuery(id+"F0.wireOp",EDGE,"E24"),sQuery(id+"F0.wireOp",EDGE,"E25"),sQuery(id+"F0.wireOp",EDGE,"E26"),sQuery(id+"F0.wireOp",EDGE,"E27"),sQuery(id+"F0.wireOp",EDGE,"E28"),sQuery(id+"F0.wireOp",EDGE,"E29"),sQuery(id+"F0.wireOp",EDGE,"E30"),sQuery(id+"F0.wireOp",EDGE,"E31"),sQuery(id+"F0.wireOp",EDGE,"E32"),sQuery(id+"F0.wireOp",EDGE,"E33"),sQuery(id+"F0.wireOp",EDGE,"E34"),sQuery(id+"F0.wireOp",EDGE,"E35"),sQuery(id+"F0.wireOp",EDGE,"E36"),sQuery(id+"F0.wireOp",EDGE,"E37"),sQuery(id+"F0.wireOp",EDGE,"E38"),sQuery(id+"F0.wireOp",EDGE,"E39"),sQuery(id+"F0.wireOp",EDGE,"E40"),sQuery(id+"F0.wireOp",EDGE,"E41"),sQuery(id+"F0.wireOp",EDGE,"E42"),sQuery(id+"F0.wireOp",EDGE,"E43"),sQuery(id+"F0.wireOp",EDGE,"E44"),sQuery(id+"F0.wireOp",EDGE,"E45"),sQuery(id+"F0.wireOp",EDGE,"E46"),sQuery(id+"F0.wireOp",EDGE,"E47"),sQuery(id+"F0.wireOp",EDGE,"E48"),sQuery(id+"F0.wireOp",EDGE,"E49"),sQuery(id+"F0.wireOp",EDGE,"E50"),sQuery(id+"F0.wireOp",EDGE,"E51"),sQuery(id+"F0.wireOp",EDGE,"E52"),sQuery(id+"F0.wireOp",EDGE,"E53"),sQuery(id+"F0.wireOp",EDGE,"E54"),sQuery(id+"F0.wireOp",EDGE,"E55"),sQuery(id+"F0.wireOp",EDGE,"E56"),sQuery(id+"F0.wireOp",EDGE,"E57"),sQuery(id+"F0.wireOp",EDGE,"E58"),sQuery(id+"F0.wireOp",EDGE,"E59"),sQuery(id+"F0.wireOp",EDGE,"E60"),sQuery(id+"F0.wireOp",EDGE,"E61"),sQuery(id+"F0.wireOp",EDGE,"E62"),sQuery(id+"F0.wireOp",EDGE,"E63"),sQuery(id+"F0.wireOp",EDGE,"E64"),sQuery(id+"F0.wireOp",EDGE,"E65"),sQuery(id+"F0.wireOp",EDGE,"E66"),sQuery(id+"F0.wireOp",EDGE,"E67"),sQuery(id+"F0.wireOp",EDGE,"E68"),sQuery(id+"F0.wireOp",EDGE,"E69"),sQuery(id+"F0.wireOp",EDGE,"E70"),sQuery(id+"F0.wireOp",EDGE,"E71"),sQuery(id+"F0.wireOp",EDGE,"E72"),sQuery(id+"F0.wireOp",EDGE,"E73"),sQuery(id+"F0.wireOp",EDGE,"E74"),sQuery(id+"F0.wireOp",EDGE,"E75"),sQuery(id+"F0.wireOp",EDGE,"E76"),sQuery(id+"F0.wireOp",EDGE,"E77"),sQuery(id+"F0.wireOp",EDGE,"E78"),sQuery(id+"F0.wireOp",EDGE,"E79"),sQuery(id+"F0.wireOp",EDGE,"E80"),sQuery(id+"F0.wireOp",EDGE,"E81"),sQuery(id+"F0.wireOp",EDGE,"E82"),sQuery(id+"F0.wireOp",EDGE,"E83"),sQuery(id+"F0.wireOp",EDGE,"E84"),sQuery(id+"F0.wireOp",EDGE,"E85"),sQuery(id+"F0.wireOp",EDGE,"E86"),sQuery(id+"F0.wireOp",EDGE,"E87"),sQuery(id+"F0.wireOp",EDGE,"E88"),sQuery(id+"F0.wireOp",EDGE,"E89"),sQuery(id+"F0.wireOp",EDGE,"E90")])]});
            var Q1;
            Q1=qCreatedBy(makeId("Origin.pointOp"),VERTEX);
            transform(context, id + "F14", {"entities" : qUnion([Q0]), "transformType" : TransformType.SCALE_UNIFORMLY, "scale" : 1.5, "scalePoint" : qUnion([Q1]), "makeCopy" : false});
        }
        {
            var Q0;
            Q0=qCreatedBy(makeId("Front.planeOp"),FACE);
            cPlane(context, id + "F15", {"entities" : qUnion([Q0]), "cplaneType" : CPlaneType.OFFSET, "offset" : 25 * mm, "width" : 150 * mm, "height" : 150 * mm});
        }
        {
            var Q0;
            Q0=qCreatedBy(id+"F15.planeOp",FACE);
            var sketch = newSketch(context, id + "F16", { "sketchPlane" : qUnion([Q0])});
            skLineSegment(sketch, "E223", {"start": v(0, 0) * mm, "end": v(0, 5) * mm, "construction": true});
            skLineSegment(sketch, "E224.bottom", {"start": v(-37.33, 19.45) * mm, "end": v(36.8, 22.36) * mm});
            skLineSegment(sketch, "E224.left", {"start": v(-37.33, 19.45) * mm, "end": v(-37.33, 5) * mm});
            skLineSegment(sketch, "E224.right", {"start": v(36.8, 22.36) * mm, "end": v(36.8, 5) * mm});
            skPoint(sketch, "E224.middle", {"position": v(0, 5) * mm});
            skLineSegment(sketch, "E225", {"start": v(0, 5) * mm, "end": v(-37.33, 5) * mm});
            skLineSegment(sketch, "E226", {"start": v(0, 5) * mm, "end": v(36.8, 5) * mm});
            skSolve(sketch);
        }
        {
            var Q0;
            Q0=makeQuery(id+"F16.imprint","IMPRINT",FACE,{"disambiguationData":[TD([[makeQuery(id+"F16.imprint","IMPRINT",EDGE,{"derivedFrom":sQuery(id+"F16.wireOp",EDGE,"E224.bottom")}),-1.0]])]});
            extrude(context, id + "F17", {"entities" : qUnion([Q0]), "operationType" : NewBodyOperationType.REMOVE, "oppositeDirection" : true, "depth" : 100 * mm});
        }
        {
            var Q0;
            Q0=makeQuery(id+"F17.boolean.opBoolean","COPY",FACE,{"derivedFrom":makeQuery(id+"F17.opExtrude","SWEPT_FACE",FACE,{"disambiguationData":[OSD([sQuery(id+"F16.wireOp",EDGE,"E225"),sQuery(id+"F16.wireOp",EDGE,"E226")])]})});
            var sketch = newSketch(context, id + "F18", { "sketchPlane" : qUnion([Q0])});
            skArc(sketch, "E227", {"start": v(16.08, 13.18) * mm, "mid": v(16.2, 13.24) * mm, "end": v(16.23, 13.36) * mm});
            skArc(sketch, "E228", {"start": v(14.97, 13.73) * mm, "mid": v(14.85, 13.66) * mm, "end": v(14.8, 13.54) * mm});
            skLineSegment(sketch, "E229", {"start": v(16.23, 13.36) * mm, "end": v(14.97, 13.73) * mm});
            skLineSegment(sketch, "E230", {"start": v(14.8, 13.54) * mm, "end": v(16.08, 13.18) * mm});
            skSolve(sketch);
        }
        {
            var Q0;
            {var subQ0=sQuery(id+"F18.wireOp",EDGE,"E227");Q0=makeQuery(id+"F18.imprint","IMPRINT",FACE,{"disambiguationData":[TD([[makeQuery(id+"F18.imprint","IMPRINT",EDGE,{"derivedFrom":subQ0}),1.0]])]});}
            extrude(context, id + "F19", {"entities" : qUnion([Q0]), "operationType" : NewBodyOperationType.ADD, "oppositeDirection" : true, "depth" : 5 * mm});
        }
    });
